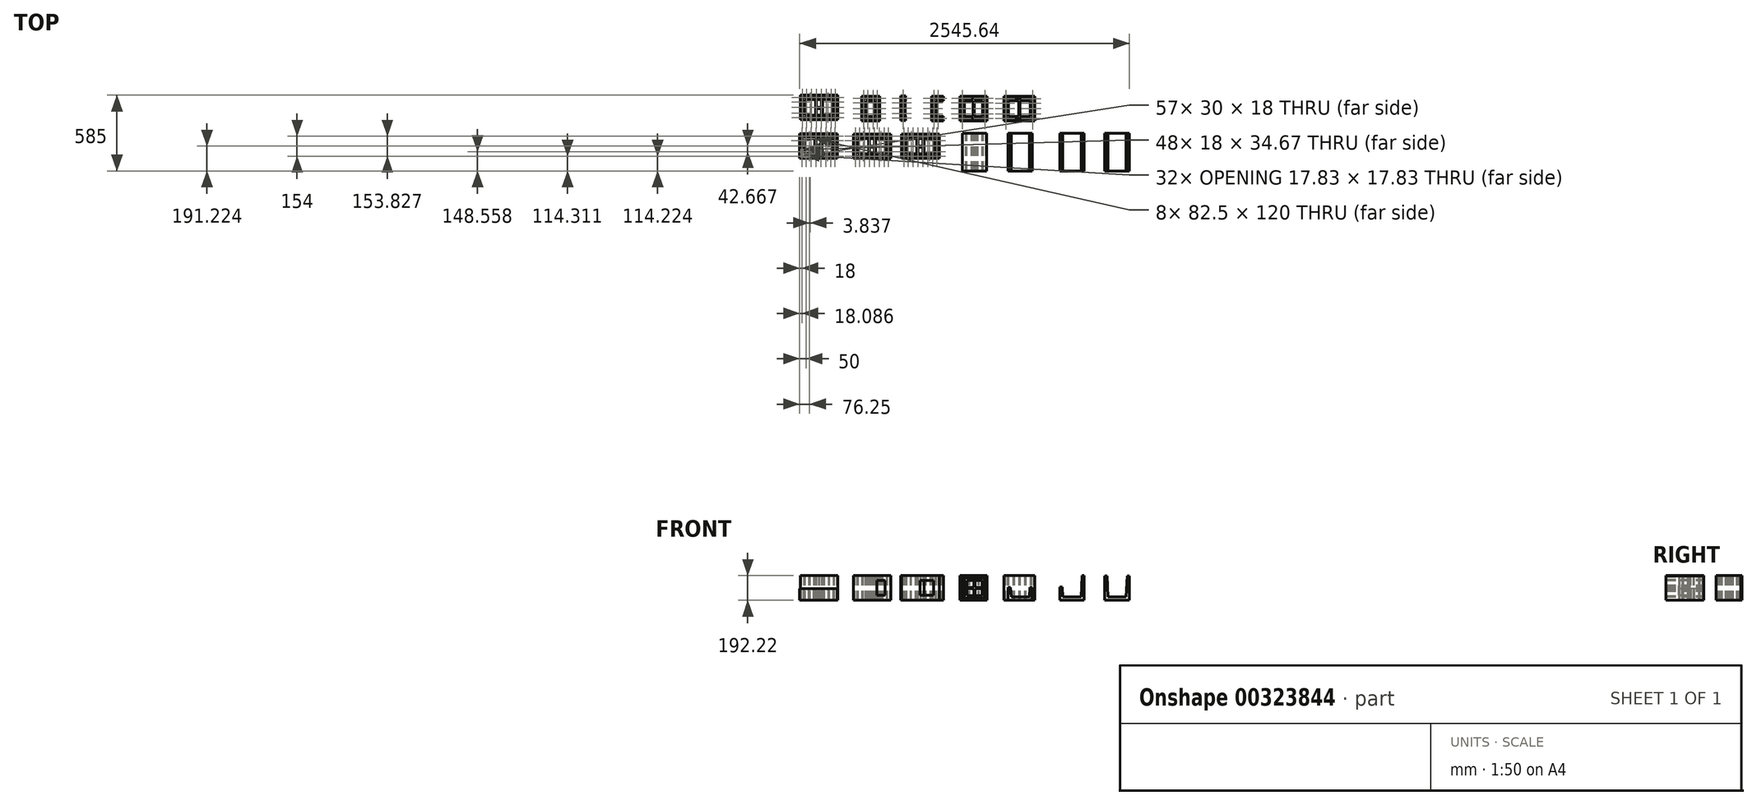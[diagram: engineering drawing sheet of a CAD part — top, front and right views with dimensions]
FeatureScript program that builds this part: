
annotation { "Feature Type Name" : "Feature", "Feature Type Description" : "" }
export const myFeature = defineFeature(function(context is Context, id is Id, definition is map)
    precondition{}
    {
        {
            var Q0;
            Q0=qCreatedBy(makeId("Top.planeOp"),FACE);
            var sketch = newSketch(context, id + "F0", { "sketchPlane" : qUnion([Q0])});
            skLineSegment(sketch, "E0", {"start": v(-906.96, 97) * mm, "end": v(-906.96, -93) * mm});
            skLineSegment(sketch, "E1", {"start": v(-906.96, -93) * mm, "end": v(-616.96, -93) * mm});
            skLineSegment(sketch, "E2", {"start": v(-616.96, -93) * mm, "end": v(-616.96, 97) * mm});
            skLineSegment(sketch, "E3", {"start": v(-616.96, 97) * mm, "end": v(-906.96, 97) * mm});
            skLineSegment(sketch, "E4", {"start": v(-871.96, 88) * mm, "end": v(-871.96, 70) * mm});
            skLineSegment(sketch, "E5", {"start": v(-871.96, 70) * mm, "end": v(-841.96, 70) * mm});
            skLineSegment(sketch, "E6", {"start": v(-841.96, 70) * mm, "end": v(-841.96, 88) * mm});
            skLineSegment(sketch, "E7", {"start": v(-841.96, 88) * mm, "end": v(-871.96, 88) * mm});
            skLineSegment(sketch, "E8", {"start": v(-833.96, 88) * mm, "end": v(-833.96, 70) * mm});
            skLineSegment(sketch, "E9", {"start": v(-833.96, 70) * mm, "end": v(-803.96, 70) * mm});
            skLineSegment(sketch, "E10", {"start": v(-803.96, 70) * mm, "end": v(-803.96, 88) * mm});
            skLineSegment(sketch, "E11", {"start": v(-803.96, 88) * mm, "end": v(-833.96, 88) * mm});
            skLineSegment(sketch, "E12", {"start": v(-795.96, 88) * mm, "end": v(-795.96, 70) * mm});
            skLineSegment(sketch, "E13", {"start": v(-795.96, 70) * mm, "end": v(-765.96, 70) * mm});
            skLineSegment(sketch, "E14", {"start": v(-765.96, 70) * mm, "end": v(-765.96, 88) * mm});
            skLineSegment(sketch, "E15", {"start": v(-765.96, 88) * mm, "end": v(-795.96, 88) * mm});
            skLineSegment(sketch, "E16", {"start": v(-757.96, 88) * mm, "end": v(-757.96, 70) * mm});
            skLineSegment(sketch, "E17", {"start": v(-757.96, 70) * mm, "end": v(-727.96, 70) * mm});
            skLineSegment(sketch, "E18", {"start": v(-727.96, 70) * mm, "end": v(-727.96, 88) * mm});
            skLineSegment(sketch, "E19", {"start": v(-727.96, 88) * mm, "end": v(-757.96, 88) * mm});
            skLineSegment(sketch, "E20", {"start": v(-719.96, 88) * mm, "end": v(-719.96, 70) * mm});
            skLineSegment(sketch, "E21", {"start": v(-719.96, 70) * mm, "end": v(-689.96, 70) * mm});
            skLineSegment(sketch, "E22", {"start": v(-689.96, 70) * mm, "end": v(-689.96, 88) * mm});
            skLineSegment(sketch, "E23", {"start": v(-689.96, 88) * mm, "end": v(-719.96, 88) * mm});
            skLineSegment(sketch, "E24", {"start": v(-681.96, 88) * mm, "end": v(-681.96, 70) * mm});
            skLineSegment(sketch, "E25", {"start": v(-681.96, 70) * mm, "end": v(-651.96, 70) * mm});
            skLineSegment(sketch, "E26", {"start": v(-651.96, 70) * mm, "end": v(-651.96, 88) * mm});
            skLineSegment(sketch, "E27", {"start": v(-651.96, 88) * mm, "end": v(-681.96, 88) * mm});
            skLineSegment(sketch, "E28", {"start": v(-643.96, 62) * mm, "end": v(-643.96, 27.33) * mm});
            skLineSegment(sketch, "E29", {"start": v(-643.96, 27.33) * mm, "end": v(-625.96, 27.33) * mm});
            skLineSegment(sketch, "E30", {"start": v(-625.96, 27.33) * mm, "end": v(-625.96, 62) * mm});
            skLineSegment(sketch, "E31", {"start": v(-625.96, 62) * mm, "end": v(-643.96, 62) * mm});
            skLineSegment(sketch, "E32", {"start": v(-897.96, 62) * mm, "end": v(-897.96, 27.33) * mm});
            skLineSegment(sketch, "E33", {"start": v(-897.96, 27.33) * mm, "end": v(-879.96, 27.33) * mm});
            skLineSegment(sketch, "E34", {"start": v(-879.96, 27.33) * mm, "end": v(-879.96, 62) * mm});
            skLineSegment(sketch, "E35", {"start": v(-879.96, 62) * mm, "end": v(-897.96, 62) * mm});
            skLineSegment(sketch, "E36", {"start": v(-897.96, 19.33) * mm, "end": v(-897.96, -15.33) * mm});
            skLineSegment(sketch, "E37", {"start": v(-897.96, -15.33) * mm, "end": v(-879.96, -15.33) * mm});
            skLineSegment(sketch, "E38", {"start": v(-879.96, -15.33) * mm, "end": v(-879.96, 19.33) * mm});
            skLineSegment(sketch, "E39", {"start": v(-879.96, 19.33) * mm, "end": v(-897.96, 19.33) * mm});
            skLineSegment(sketch, "E40", {"start": v(-897.96, -23.33) * mm, "end": v(-897.96, -58) * mm});
            skLineSegment(sketch, "E41", {"start": v(-897.96, -58) * mm, "end": v(-879.96, -58) * mm});
            skLineSegment(sketch, "E42", {"start": v(-879.96, -58) * mm, "end": v(-879.96, -23.33) * mm});
            skLineSegment(sketch, "E43", {"start": v(-879.96, -23.33) * mm, "end": v(-897.96, -23.33) * mm});
            skLineSegment(sketch, "E44", {"start": v(-871.96, -66) * mm, "end": v(-871.96, -84) * mm});
            skLineSegment(sketch, "E45", {"start": v(-871.96, -84) * mm, "end": v(-841.96, -84) * mm});
            skLineSegment(sketch, "E46", {"start": v(-841.96, -84) * mm, "end": v(-841.96, -66) * mm});
            skLineSegment(sketch, "E47", {"start": v(-841.96, -66) * mm, "end": v(-871.96, -66) * mm});
            skLineSegment(sketch, "E48", {"start": v(-833.96, -66) * mm, "end": v(-833.96, -84) * mm});
            skLineSegment(sketch, "E49", {"start": v(-833.96, -84) * mm, "end": v(-803.96, -84) * mm});
            skLineSegment(sketch, "E50", {"start": v(-803.96, -84) * mm, "end": v(-803.96, -66) * mm});
            skLineSegment(sketch, "E51", {"start": v(-803.96, -66) * mm, "end": v(-833.96, -66) * mm});
            skLineSegment(sketch, "E52", {"start": v(-871.96, 62) * mm, "end": v(-871.96, -58) * mm});
            skLineSegment(sketch, "E53", {"start": v(-871.96, -58) * mm, "end": v(-789.46, -58) * mm});
            skLineSegment(sketch, "E54", {"start": v(-789.46, -58) * mm, "end": v(-789.46, 62) * mm});
            skLineSegment(sketch, "E55", {"start": v(-789.46, 62) * mm, "end": v(-871.96, 62) * mm});
            skLineSegment(sketch, "E56", {"start": v(-795.96, -66) * mm, "end": v(-795.96, -84) * mm});
            skLineSegment(sketch, "E57", {"start": v(-795.96, -84) * mm, "end": v(-765.96, -84) * mm});
            skLineSegment(sketch, "E58", {"start": v(-765.96, -84) * mm, "end": v(-765.96, -66) * mm});
            skLineSegment(sketch, "E59", {"start": v(-765.96, -66) * mm, "end": v(-795.96, -66) * mm});
            skLineSegment(sketch, "E60", {"start": v(-757.96, -66) * mm, "end": v(-757.96, -84) * mm});
            skLineSegment(sketch, "E61", {"start": v(-757.96, -84) * mm, "end": v(-727.96, -84) * mm});
            skLineSegment(sketch, "E62", {"start": v(-727.96, -84) * mm, "end": v(-727.96, -66) * mm});
            skLineSegment(sketch, "E63", {"start": v(-727.96, -66) * mm, "end": v(-757.96, -66) * mm});
            skLineSegment(sketch, "E64", {"start": v(-719.96, -66) * mm, "end": v(-719.96, -84) * mm});
            skLineSegment(sketch, "E65", {"start": v(-719.96, -84) * mm, "end": v(-689.96, -84) * mm});
            skLineSegment(sketch, "E66", {"start": v(-689.96, -84) * mm, "end": v(-689.96, -66) * mm});
            skLineSegment(sketch, "E67", {"start": v(-689.96, -66) * mm, "end": v(-719.96, -66) * mm});
            skLineSegment(sketch, "E68", {"start": v(-681.96, -66) * mm, "end": v(-681.96, -84) * mm});
            skLineSegment(sketch, "E69", {"start": v(-681.96, -84) * mm, "end": v(-651.96, -84) * mm});
            skLineSegment(sketch, "E70", {"start": v(-651.96, -84) * mm, "end": v(-651.96, -66) * mm});
            skLineSegment(sketch, "E71", {"start": v(-651.96, -66) * mm, "end": v(-681.96, -66) * mm});
            skLineSegment(sketch, "E72", {"start": v(-643.96, -58) * mm, "end": v(-643.96, -23.33) * mm});
            skLineSegment(sketch, "E73", {"start": v(-643.96, -23.33) * mm, "end": v(-625.96, -23.33) * mm});
            skLineSegment(sketch, "E74", {"start": v(-625.96, -23.33) * mm, "end": v(-625.96, -58) * mm});
            skLineSegment(sketch, "E75", {"start": v(-625.96, -58) * mm, "end": v(-643.96, -58) * mm});
            skLineSegment(sketch, "E76", {"start": v(-625.96, -15.33) * mm, "end": v(-625.96, 19.33) * mm});
            skLineSegment(sketch, "E77", {"start": v(-625.96, 19.33) * mm, "end": v(-643.96, 19.33) * mm});
            skLineSegment(sketch, "E78", {"start": v(-643.96, 19.33) * mm, "end": v(-643.96, -15.33) * mm});
            skLineSegment(sketch, "E79", {"start": v(-643.96, -15.33) * mm, "end": v(-625.96, -15.33) * mm});
            skLineSegment(sketch, "E80", {"start": v(-734.46, 62) * mm, "end": v(-734.46, -58) * mm});
            skLineSegment(sketch, "E81", {"start": v(-734.46, -58) * mm, "end": v(-651.96, -58) * mm});
            skLineSegment(sketch, "E82", {"start": v(-651.96, -58) * mm, "end": v(-651.96, 62) * mm});
            skLineSegment(sketch, "E83", {"start": v(-651.96, 62) * mm, "end": v(-734.46, 62) * mm});
            skLineSegment(sketch, "E84", {"start": v(-742.46, -58) * mm, "end": v(-742.46, -6) * mm});
            skLineSegment(sketch, "E85", {"start": v(-742.46, -6) * mm, "end": v(-781.46, -6) * mm});
            skLineSegment(sketch, "E86", {"start": v(-781.46, -6) * mm, "end": v(-781.46, -58) * mm});
            skLineSegment(sketch, "E87", {"start": v(-781.46, -58) * mm, "end": v(-742.46, -58) * mm});
            skLineSegment(sketch, "E88", {"start": v(-781.46, 62) * mm, "end": v(-781.46, 2) * mm});
            skLineSegment(sketch, "E89", {"start": v(-781.46, 2) * mm, "end": v(-742.46, 2) * mm});
            skLineSegment(sketch, "E90", {"start": v(-742.46, 2) * mm, "end": v(-742.46, 62) * mm});
            skLineSegment(sketch, "E91", {"start": v(-742.46, 62) * mm, "end": v(-781.46, 62) * mm});
            skLineSegment(sketch, "E92", {"start": v(-433.37, 89.63) * mm, "end": v(-433.37, -100.37) * mm});
            skLineSegment(sketch, "E93", {"start": v(-433.37, -100.37) * mm, "end": v(-293.37, -100.37) * mm});
            skLineSegment(sketch, "E94", {"start": v(-293.37, -100.37) * mm, "end": v(-293.37, 89.63) * mm});
            skLineSegment(sketch, "E95", {"start": v(-293.37, 89.63) * mm, "end": v(-433.37, 89.63) * mm});
            skLineSegment(sketch, "E96", {"start": v(-424.37, 54.63) * mm, "end": v(-424.37, 19.96) * mm});
            skLineSegment(sketch, "E97", {"start": v(-424.37, 19.96) * mm, "end": v(-406.37, 19.96) * mm});
            skLineSegment(sketch, "E98", {"start": v(-406.37, 19.96) * mm, "end": v(-406.37, 54.63) * mm});
            skLineSegment(sketch, "E99", {"start": v(-406.37, 54.63) * mm, "end": v(-424.37, 54.63) * mm});
            skLineSegment(sketch, "E100", {"start": v(-424.37, 11.96) * mm, "end": v(-424.37, -22.7) * mm});
            skLineSegment(sketch, "E101", {"start": v(-424.37, -22.7) * mm, "end": v(-406.37, -22.7) * mm});
            skLineSegment(sketch, "E102", {"start": v(-406.37, -22.7) * mm, "end": v(-406.37, 11.96) * mm});
            skLineSegment(sketch, "E103", {"start": v(-406.37, 11.96) * mm, "end": v(-424.37, 11.96) * mm});
            skLineSegment(sketch, "E104", {"start": v(-424.37, -30.7) * mm, "end": v(-424.37, -65.37) * mm});
            skLineSegment(sketch, "E105", {"start": v(-424.37, -65.37) * mm, "end": v(-406.37, -65.37) * mm});
            skLineSegment(sketch, "E106", {"start": v(-406.37, -65.37) * mm, "end": v(-406.37, -30.7) * mm});
            skLineSegment(sketch, "E107", {"start": v(-406.37, -30.7) * mm, "end": v(-424.37, -30.7) * mm});
            skLineSegment(sketch, "E108", {"start": v(-398.37, -73.37) * mm, "end": v(-398.37, -91.37) * mm});
            skLineSegment(sketch, "E109", {"start": v(-398.37, -91.37) * mm, "end": v(-368.37, -91.37) * mm});
            skLineSegment(sketch, "E110", {"start": v(-368.37, -91.37) * mm, "end": v(-368.37, -73.37) * mm});
            skLineSegment(sketch, "E111", {"start": v(-368.37, -73.37) * mm, "end": v(-398.37, -73.37) * mm});
            skLineSegment(sketch, "E112", {"start": v(-358.37, -73.37) * mm, "end": v(-358.37, -91.37) * mm});
            skLineSegment(sketch, "E113", {"start": v(-358.37, -91.37) * mm, "end": v(-328.37, -91.37) * mm});
            skLineSegment(sketch, "E114", {"start": v(-328.37, -91.37) * mm, "end": v(-328.37, -73.37) * mm});
            skLineSegment(sketch, "E115", {"start": v(-328.37, -73.37) * mm, "end": v(-358.37, -73.37) * mm});
            skLineSegment(sketch, "E116", {"start": v(-320.37, 54.63) * mm, "end": v(-320.37, 19.96) * mm});
            skLineSegment(sketch, "E117", {"start": v(-320.37, 19.96) * mm, "end": v(-302.37, 19.96) * mm});
            skLineSegment(sketch, "E118", {"start": v(-302.37, 19.96) * mm, "end": v(-302.37, 54.63) * mm});
            skLineSegment(sketch, "E119", {"start": v(-302.37, 54.63) * mm, "end": v(-320.37, 54.63) * mm});
            skLineSegment(sketch, "E120", {"start": v(-320.37, 11.96) * mm, "end": v(-320.37, -22.7) * mm});
            skLineSegment(sketch, "E121", {"start": v(-320.37, -22.7) * mm, "end": v(-302.37, -22.7) * mm});
            skLineSegment(sketch, "E122", {"start": v(-302.37, -22.7) * mm, "end": v(-302.37, 11.96) * mm});
            skLineSegment(sketch, "E123", {"start": v(-302.37, 11.96) * mm, "end": v(-320.37, 11.96) * mm});
            skLineSegment(sketch, "E124", {"start": v(-320.37, -30.7) * mm, "end": v(-320.37, -65.37) * mm});
            skLineSegment(sketch, "E125", {"start": v(-320.37, -65.37) * mm, "end": v(-302.37, -65.37) * mm});
            skLineSegment(sketch, "E126", {"start": v(-302.37, -65.37) * mm, "end": v(-302.37, -30.7) * mm});
            skLineSegment(sketch, "E127", {"start": v(-302.37, -30.7) * mm, "end": v(-320.37, -30.7) * mm});
            skLineSegment(sketch, "E128", {"start": v(-398.37, 54.63) * mm, "end": v(-398.37, -65.37) * mm});
            skLineSegment(sketch, "E129", {"start": v(-398.37, -65.37) * mm, "end": v(-328.37, -65.37) * mm});
            skLineSegment(sketch, "E130", {"start": v(-328.37, -65.37) * mm, "end": v(-328.37, 54.63) * mm});
            skLineSegment(sketch, "E131", {"start": v(-328.37, 54.63) * mm, "end": v(-398.37, 54.63) * mm});
            skLineSegment(sketch, "E132", {"start": v(-398.37, 80.63) * mm, "end": v(-398.37, 62.63) * mm});
            skLineSegment(sketch, "E133", {"start": v(-398.37, 62.63) * mm, "end": v(-368.37, 62.63) * mm});
            skLineSegment(sketch, "E134", {"start": v(-368.37, 62.63) * mm, "end": v(-368.37, 80.63) * mm});
            skLineSegment(sketch, "E135", {"start": v(-368.37, 80.63) * mm, "end": v(-398.37, 80.63) * mm});
            skLineSegment(sketch, "E136", {"start": v(-358.37, 62.63) * mm, "end": v(-358.37, 80.63) * mm});
            skLineSegment(sketch, "E137", {"start": v(-358.37, 80.63) * mm, "end": v(-328.37, 80.63) * mm});
            skLineSegment(sketch, "E138", {"start": v(-328.37, 80.63) * mm, "end": v(-328.37, 62.63) * mm});
            skLineSegment(sketch, "E139", {"start": v(-328.37, 62.63) * mm, "end": v(-358.37, 62.63) * mm});
            skLineSegment(sketch, "E140", {"start": v(-122.36, 56.55) * mm, "end": v(-122.36, 21.88) * mm});
            skLineSegment(sketch, "E141", {"start": v(-122.36, 21.88) * mm, "end": v(-104.36, 21.88) * mm});
            skLineSegment(sketch, "E142", {"start": v(-104.36, 21.88) * mm, "end": v(-104.36, 56.55) * mm});
            skLineSegment(sketch, "E143", {"start": v(-104.36, 56.55) * mm, "end": v(-122.36, 56.55) * mm});
            skLineSegment(sketch, "E144", {"start": v(-122.36, 13.88) * mm, "end": v(-122.36, -20.78) * mm});
            skLineSegment(sketch, "E145", {"start": v(-122.36, -20.78) * mm, "end": v(-104.36, -20.78) * mm});
            skLineSegment(sketch, "E146", {"start": v(-104.36, -20.78) * mm, "end": v(-104.36, 13.88) * mm});
            skLineSegment(sketch, "E147", {"start": v(-104.36, 13.88) * mm, "end": v(-122.36, 13.88) * mm});
            skLineSegment(sketch, "E148", {"start": v(-122.36, -28.78) * mm, "end": v(-122.36, -63.45) * mm});
            skLineSegment(sketch, "E149", {"start": v(-122.36, -63.45) * mm, "end": v(-104.36, -63.45) * mm});
            skLineSegment(sketch, "E150", {"start": v(-104.36, -63.45) * mm, "end": v(-104.36, -28.78) * mm});
            skLineSegment(sketch, "E151", {"start": v(-104.36, -28.78) * mm, "end": v(-122.36, -28.78) * mm});
            skLineSegment(sketch, "E152", {"start": v(-131.36, -98.45) * mm, "end": v(-131.36, 91.55) * mm});
            skLineSegment(sketch, "E153", {"start": v(-131.36, 91.55) * mm, "end": v(-91.36, 91.55) * mm});
            skLineSegment(sketch, "E154", {"start": v(-91.36, 91.55) * mm, "end": v(-91.36, 82.55) * mm});
            skLineSegment(sketch, "E155", {"start": v(-91.36, 82.55) * mm, "end": v(-96.36, 82.55) * mm});
            skLineSegment(sketch, "E156", {"start": v(-96.36, 82.55) * mm, "end": v(-96.36, 64.55) * mm});
            skLineSegment(sketch, "E157", {"start": v(-96.36, 64.55) * mm, "end": v(-91.36, 64.55) * mm});
            skLineSegment(sketch, "E158", {"start": v(-91.36, 64.55) * mm, "end": v(-91.36, 56.55) * mm});
            skLineSegment(sketch, "E159", {"start": v(-91.36, 56.55) * mm, "end": v(-96.36, 56.55) * mm});
            skLineSegment(sketch, "E160", {"start": v(-96.36, 56.55) * mm, "end": v(-96.36, -63.45) * mm});
            skLineSegment(sketch, "E161", {"start": v(-96.36, -63.45) * mm, "end": v(-91.36, -63.45) * mm});
            skLineSegment(sketch, "E162", {"start": v(-91.36, -63.45) * mm, "end": v(-91.36, -71.45) * mm});
            skLineSegment(sketch, "E163", {"start": v(-91.36, -71.45) * mm, "end": v(-96.36, -71.45) * mm});
            skLineSegment(sketch, "E164", {"start": v(-96.36, -71.45) * mm, "end": v(-96.36, -89.45) * mm});
            skLineSegment(sketch, "E165", {"start": v(-96.36, -89.45) * mm, "end": v(-91.36, -89.45) * mm});
            skLineSegment(sketch, "E166", {"start": v(-91.36, -89.45) * mm, "end": v(-91.36, -98.45) * mm});
            skLineSegment(sketch, "E167", {"start": v(-91.36, -98.45) * mm, "end": v(-131.36, -98.45) * mm});
            skLineSegment(sketch, "E168", {"start": v(198.64, 89.49) * mm, "end": v(108.64, 89.49) * mm});
            skLineSegment(sketch, "E169", {"start": v(108.64, 89.49) * mm, "end": v(108.64, -100.51) * mm});
            skLineSegment(sketch, "E170", {"start": v(108.64, -100.51) * mm, "end": v(198.64, -100.51) * mm});
            skLineSegment(sketch, "E171", {"start": v(198.64, -100.51) * mm, "end": v(198.64, -91.51) * mm});
            skLineSegment(sketch, "E172", {"start": v(198.64, -91.51) * mm, "end": v(181.64, -91.51) * mm});
            skLineSegment(sketch, "E173", {"start": v(181.64, -91.51) * mm, "end": v(181.64, -73.51) * mm});
            skLineSegment(sketch, "E174", {"start": v(181.64, -73.51) * mm, "end": v(198.64, -73.51) * mm});
            skLineSegment(sketch, "E175", {"start": v(198.64, -73.51) * mm, "end": v(198.64, -65.51) * mm});
            skLineSegment(sketch, "E176", {"start": v(198.64, -65.51) * mm, "end": v(143.64, -65.51) * mm});
            skLineSegment(sketch, "E177", {"start": v(143.64, -65.51) * mm, "end": v(143.64, 54.49) * mm});
            skLineSegment(sketch, "E178", {"start": v(143.64, 54.49) * mm, "end": v(198.64, 54.49) * mm});
            skLineSegment(sketch, "E179", {"start": v(198.64, 54.49) * mm, "end": v(198.64, 62.49) * mm});
            skLineSegment(sketch, "E180", {"start": v(198.64, 62.49) * mm, "end": v(181.64, 62.49) * mm});
            skLineSegment(sketch, "E181", {"start": v(181.64, 62.49) * mm, "end": v(181.64, 80.49) * mm});
            skLineSegment(sketch, "E182", {"start": v(181.64, 80.49) * mm, "end": v(198.64, 80.49) * mm});
            skLineSegment(sketch, "E183", {"start": v(198.64, 80.49) * mm, "end": v(198.64, 89.49) * mm});
            skLineSegment(sketch, "E184", {"start": v(143.64, 80.49) * mm, "end": v(143.64, 62.49) * mm});
            skLineSegment(sketch, "E185", {"start": v(143.64, 62.49) * mm, "end": v(173.64, 62.49) * mm});
            skLineSegment(sketch, "E186", {"start": v(173.64, 62.49) * mm, "end": v(173.64, 80.49) * mm});
            skLineSegment(sketch, "E187", {"start": v(173.64, 80.49) * mm, "end": v(143.64, 80.49) * mm});
            skLineSegment(sketch, "E188", {"start": v(117.64, 54.49) * mm, "end": v(117.64, 19.82) * mm});
            skLineSegment(sketch, "E189", {"start": v(117.64, 19.82) * mm, "end": v(135.64, 19.82) * mm});
            skLineSegment(sketch, "E190", {"start": v(135.64, 19.82) * mm, "end": v(135.64, 54.49) * mm});
            skLineSegment(sketch, "E191", {"start": v(135.64, 54.49) * mm, "end": v(117.64, 54.49) * mm});
            skLineSegment(sketch, "E192", {"start": v(117.64, 11.82) * mm, "end": v(117.64, -22.85) * mm});
            skLineSegment(sketch, "E193", {"start": v(117.64, -22.85) * mm, "end": v(135.64, -22.85) * mm});
            skLineSegment(sketch, "E194", {"start": v(135.64, -22.85) * mm, "end": v(135.64, 11.82) * mm});
            skLineSegment(sketch, "E195", {"start": v(135.64, 11.82) * mm, "end": v(117.64, 11.82) * mm});
            skLineSegment(sketch, "E196", {"start": v(117.64, -30.85) * mm, "end": v(117.64, -65.51) * mm});
            skLineSegment(sketch, "E197", {"start": v(117.64, -65.51) * mm, "end": v(135.64, -65.51) * mm});
            skLineSegment(sketch, "E198", {"start": v(135.64, -65.51) * mm, "end": v(135.64, -30.85) * mm});
            skLineSegment(sketch, "E199", {"start": v(135.64, -30.85) * mm, "end": v(117.64, -30.85) * mm});
            skLineSegment(sketch, "E200", {"start": v(143.64, -73.51) * mm, "end": v(143.64, -91.51) * mm});
            skLineSegment(sketch, "E201", {"start": v(143.64, -91.51) * mm, "end": v(173.64, -91.51) * mm});
            skLineSegment(sketch, "E202", {"start": v(173.64, -91.51) * mm, "end": v(173.64, -73.51) * mm});
            skLineSegment(sketch, "E203", {"start": v(173.64, -73.51) * mm, "end": v(143.64, -73.51) * mm});
            skLineSegment(sketch, "E204", {"start": v(327.12, 89.6) * mm, "end": v(327.12, -100.4) * mm});
            skLineSegment(sketch, "E205", {"start": v(327.12, -100.4) * mm, "end": v(537.12, -100.4) * mm});
            skLineSegment(sketch, "E206", {"start": v(537.12, -100.4) * mm, "end": v(537.12, 89.6) * mm});
            skLineSegment(sketch, "E207", {"start": v(537.12, 89.6) * mm, "end": v(327.12, 89.6) * mm});
            skLineSegment(sketch, "E208", {"start": v(436.12, 54.6) * mm, "end": v(436.12, -65.4) * mm});
            skLineSegment(sketch, "E209", {"start": v(436.12, -65.4) * mm, "end": v(502.12, -65.4) * mm});
            skLineSegment(sketch, "E210", {"start": v(502.12, -65.4) * mm, "end": v(502.12, 54.6) * mm});
            skLineSegment(sketch, "E211", {"start": v(502.12, 54.6) * mm, "end": v(436.12, 54.6) * mm});
            skLineSegment(sketch, "E212", {"start": v(428.12, 54.6) * mm, "end": v(428.12, -65.4) * mm});
            skLineSegment(sketch, "E213", {"start": v(428.12, -65.4) * mm, "end": v(362.12, -65.4) * mm});
            skLineSegment(sketch, "E214", {"start": v(362.12, -65.4) * mm, "end": v(362.12, 54.6) * mm});
            skLineSegment(sketch, "E215", {"start": v(362.12, 54.6) * mm, "end": v(428.12, 54.6) * mm});
            skLineSegment(sketch, "E216", {"start": v(362.12, 80.6) * mm, "end": v(362.12, 62.6) * mm});
            skLineSegment(sketch, "E217", {"start": v(362.12, 62.6) * mm, "end": v(391.24, 62.6) * mm});
            skLineSegment(sketch, "E218", {"start": v(391.24, 62.6) * mm, "end": v(391.24, 80.6) * mm});
            skLineSegment(sketch, "E219", {"start": v(391.24, 80.6) * mm, "end": v(362.12, 80.6) * mm});
            skLineSegment(sketch, "E220", {"start": v(399, 62.6) * mm, "end": v(399, 80.6) * mm});
            skLineSegment(sketch, "E221", {"start": v(399, 80.6) * mm, "end": v(428.12, 80.6) * mm});
            skLineSegment(sketch, "E222", {"start": v(428.12, 80.6) * mm, "end": v(428.12, 62.6) * mm});
            skLineSegment(sketch, "E223", {"start": v(428.12, 62.6) * mm, "end": v(399, 62.6) * mm});
            skLineSegment(sketch, "E224", {"start": v(436.12, 80.6) * mm, "end": v(436.12, 62.6) * mm});
            skLineSegment(sketch, "E225", {"start": v(436.12, 62.6) * mm, "end": v(465.24, 62.6) * mm});
            skLineSegment(sketch, "E226", {"start": v(465.24, 62.6) * mm, "end": v(465.24, 80.6) * mm});
            skLineSegment(sketch, "E227", {"start": v(465.24, 80.6) * mm, "end": v(436.12, 80.6) * mm});
            skLineSegment(sketch, "E228", {"start": v(473, 62.6) * mm, "end": v(473, 80.6) * mm});
            skLineSegment(sketch, "E229", {"start": v(473, 80.6) * mm, "end": v(502.12, 80.6) * mm});
            skLineSegment(sketch, "E230", {"start": v(502.12, 80.6) * mm, "end": v(502.12, 62.6) * mm});
            skLineSegment(sketch, "E231", {"start": v(502.12, 62.6) * mm, "end": v(473, 62.6) * mm});
            skLineSegment(sketch, "E232", {"start": v(510.12, 54.6) * mm, "end": v(510.12, 19.93) * mm});
            skLineSegment(sketch, "E233", {"start": v(510.12, 19.93) * mm, "end": v(528.12, 19.93) * mm});
            skLineSegment(sketch, "E234", {"start": v(528.12, 19.93) * mm, "end": v(528.12, 54.6) * mm});
            skLineSegment(sketch, "E235", {"start": v(528.12, 54.6) * mm, "end": v(510.12, 54.6) * mm});
            skLineSegment(sketch, "E236", {"start": v(528.12, 11.93) * mm, "end": v(528.12, -22.74) * mm});
            skLineSegment(sketch, "E237", {"start": v(528.12, -22.74) * mm, "end": v(510.12, -22.74) * mm});
            skLineSegment(sketch, "E238", {"start": v(510.12, -22.74) * mm, "end": v(510.12, 11.93) * mm});
            skLineSegment(sketch, "E239", {"start": v(510.12, 11.93) * mm, "end": v(528.12, 11.93) * mm});
            skLineSegment(sketch, "E240", {"start": v(510.12, -30.74) * mm, "end": v(510.12, -65.4) * mm});
            skLineSegment(sketch, "E241", {"start": v(510.12, -65.4) * mm, "end": v(528.12, -65.4) * mm});
            skLineSegment(sketch, "E242", {"start": v(528.12, -65.4) * mm, "end": v(528.12, -30.74) * mm});
            skLineSegment(sketch, "E243", {"start": v(528.12, -30.74) * mm, "end": v(510.12, -30.74) * mm});
            skLineSegment(sketch, "E244", {"start": v(502.12, -73.4) * mm, "end": v(502.12, -91.4) * mm});
            skLineSegment(sketch, "E245", {"start": v(502.12, -91.4) * mm, "end": v(473, -91.4) * mm});
            skLineSegment(sketch, "E246", {"start": v(473, -91.4) * mm, "end": v(473, -73.4) * mm});
            skLineSegment(sketch, "E247", {"start": v(473, -73.4) * mm, "end": v(502.12, -73.4) * mm});
            skLineSegment(sketch, "E248", {"start": v(465.24, -91.4) * mm, "end": v(465.24, -73.4) * mm});
            skLineSegment(sketch, "E249", {"start": v(465.24, -73.4) * mm, "end": v(436.12, -73.4) * mm});
            skLineSegment(sketch, "E250", {"start": v(436.12, -73.4) * mm, "end": v(436.12, -91.4) * mm});
            skLineSegment(sketch, "E251", {"start": v(436.12, -91.4) * mm, "end": v(465.24, -91.4) * mm});
            skLineSegment(sketch, "E252", {"start": v(428.12, -91.4) * mm, "end": v(428.12, -73.4) * mm});
            skLineSegment(sketch, "E253", {"start": v(428.12, -73.4) * mm, "end": v(399, -73.4) * mm});
            skLineSegment(sketch, "E254", {"start": v(399, -73.4) * mm, "end": v(399, -91.4) * mm});
            skLineSegment(sketch, "E255", {"start": v(399, -91.4) * mm, "end": v(428.12, -91.4) * mm});
            skLineSegment(sketch, "E256", {"start": v(362.12, -73.4) * mm, "end": v(362.12, -91.4) * mm});
            skLineSegment(sketch, "E257", {"start": v(362.12, -91.4) * mm, "end": v(391.24, -91.4) * mm});
            skLineSegment(sketch, "E258", {"start": v(391.24, -91.4) * mm, "end": v(391.24, -73.4) * mm});
            skLineSegment(sketch, "E259", {"start": v(391.24, -73.4) * mm, "end": v(362.12, -73.4) * mm});
            skLineSegment(sketch, "E260", {"start": v(354.12, -65.4) * mm, "end": v(354.12, -30.74) * mm});
            skLineSegment(sketch, "E261", {"start": v(354.12, -30.74) * mm, "end": v(336.12, -30.74) * mm});
            skLineSegment(sketch, "E262", {"start": v(336.12, -30.74) * mm, "end": v(336.12, -65.4) * mm});
            skLineSegment(sketch, "E263", {"start": v(336.12, -65.4) * mm, "end": v(354.12, -65.4) * mm});
            skLineSegment(sketch, "E264", {"start": v(336.12, -22.74) * mm, "end": v(336.12, 11.93) * mm});
            skLineSegment(sketch, "E265", {"start": v(336.12, 11.93) * mm, "end": v(354.12, 11.93) * mm});
            skLineSegment(sketch, "E266", {"start": v(354.12, 11.93) * mm, "end": v(354.12, -22.74) * mm});
            skLineSegment(sketch, "E267", {"start": v(354.12, -22.74) * mm, "end": v(336.12, -22.74) * mm});
            skLineSegment(sketch, "E268", {"start": v(354.12, 19.93) * mm, "end": v(354.12, 54.6) * mm});
            skLineSegment(sketch, "E269", {"start": v(354.12, 54.6) * mm, "end": v(336.12, 54.6) * mm});
            skLineSegment(sketch, "E270", {"start": v(336.12, 54.6) * mm, "end": v(336.12, 19.93) * mm});
            skLineSegment(sketch, "E271", {"start": v(336.12, 19.93) * mm, "end": v(354.12, 19.93) * mm});
            skLineSegment(sketch, "E272", {"start": v(665.08, 88.4) * mm, "end": v(665.08, -101.6) * mm});
            skLineSegment(sketch, "E273", {"start": v(665.08, -101.6) * mm, "end": v(905.08, -101.6) * mm});
            skLineSegment(sketch, "E274", {"start": v(905.08, -101.6) * mm, "end": v(905.08, 88.4) * mm});
            skLineSegment(sketch, "E275", {"start": v(905.08, 88.4) * mm, "end": v(665.08, 88.4) * mm});
            skLineSegment(sketch, "E276", {"start": v(870.08, -66.6) * mm, "end": v(870.08, 53.4) * mm});
            skLineSegment(sketch, "E277", {"start": v(870.08, 53.4) * mm, "end": v(789.08, 53.4) * mm});
            skLineSegment(sketch, "E278", {"start": v(789.08, 53.4) * mm, "end": v(789.08, -66.6) * mm});
            skLineSegment(sketch, "E279", {"start": v(789.08, -66.6) * mm, "end": v(870.08, -66.6) * mm});
            skLineSegment(sketch, "E280", {"start": v(781.08, 53.4) * mm, "end": v(781.08, -66.6) * mm});
            skLineSegment(sketch, "E281", {"start": v(781.08, -66.6) * mm, "end": v(700.08, -66.6) * mm});
            skLineSegment(sketch, "E282", {"start": v(700.08, -66.6) * mm, "end": v(700.08, 53.4) * mm});
            skLineSegment(sketch, "E283", {"start": v(700.08, 53.4) * mm, "end": v(781.08, 53.4) * mm});
            skLineSegment(sketch, "E284", {"start": v(674.08, -66.6) * mm, "end": v(674.08, -31.94) * mm});
            skLineSegment(sketch, "E285", {"start": v(674.08, -31.94) * mm, "end": v(692.08, -31.94) * mm});
            skLineSegment(sketch, "E286", {"start": v(692.08, -31.94) * mm, "end": v(692.08, -66.6) * mm});
            skLineSegment(sketch, "E287", {"start": v(692.08, -66.6) * mm, "end": v(674.08, -66.6) * mm});
            skLineSegment(sketch, "E288", {"start": v(692.08, -23.94) * mm, "end": v(692.08, 10.73) * mm});
            skLineSegment(sketch, "E289", {"start": v(692.08, 10.73) * mm, "end": v(674.08, 10.73) * mm});
            skLineSegment(sketch, "E290", {"start": v(674.08, 10.73) * mm, "end": v(674.08, -23.94) * mm});
            skLineSegment(sketch, "E291", {"start": v(674.08, -23.94) * mm, "end": v(692.08, -23.94) * mm});
            skLineSegment(sketch, "E292", {"start": v(700.08, -74.6) * mm, "end": v(700.08, -92.6) * mm});
            skLineSegment(sketch, "E293", {"start": v(700.08, -92.6) * mm, "end": v(735.82, -92.6) * mm});
            skLineSegment(sketch, "E294", {"start": v(735.82, -92.6) * mm, "end": v(735.82, -74.6) * mm});
            skLineSegment(sketch, "E295", {"start": v(735.82, -74.6) * mm, "end": v(700.08, -74.6) * mm});
            skLineSegment(sketch, "E296", {"start": v(745.35, -74.6) * mm, "end": v(745.35, -92.6) * mm});
            skLineSegment(sketch, "E297", {"start": v(745.35, -92.6) * mm, "end": v(781.08, -92.6) * mm});
            skLineSegment(sketch, "E298", {"start": v(781.08, -92.6) * mm, "end": v(781.08, -74.6) * mm});
            skLineSegment(sketch, "E299", {"start": v(781.08, -74.6) * mm, "end": v(745.35, -74.6) * mm});
            skLineSegment(sketch, "E300", {"start": v(789.08, -74.6) * mm, "end": v(789.08, -92.6) * mm});
            skLineSegment(sketch, "E301", {"start": v(789.08, -92.6) * mm, "end": v(824.82, -92.6) * mm});
            skLineSegment(sketch, "E302", {"start": v(824.82, -92.6) * mm, "end": v(824.82, -74.6) * mm});
            skLineSegment(sketch, "E303", {"start": v(824.82, -74.6) * mm, "end": v(789.08, -74.6) * mm});
            skLineSegment(sketch, "E304", {"start": v(834.35, -74.6) * mm, "end": v(834.35, -92.6) * mm});
            skLineSegment(sketch, "E305", {"start": v(834.35, -92.6) * mm, "end": v(870.08, -92.6) * mm});
            skLineSegment(sketch, "E306", {"start": v(870.08, -92.6) * mm, "end": v(870.08, -74.6) * mm});
            skLineSegment(sketch, "E307", {"start": v(870.08, -74.6) * mm, "end": v(834.35, -74.6) * mm});
            skLineSegment(sketch, "E308", {"start": v(878.08, -31.94) * mm, "end": v(878.08, -66.6) * mm});
            skLineSegment(sketch, "E309", {"start": v(878.08, -66.6) * mm, "end": v(896.08, -66.6) * mm});
            skLineSegment(sketch, "E310", {"start": v(896.08, -66.6) * mm, "end": v(896.08, -31.94) * mm});
            skLineSegment(sketch, "E311", {"start": v(896.08, -31.94) * mm, "end": v(878.08, -31.94) * mm});
            skLineSegment(sketch, "E312", {"start": v(878.08, 10.73) * mm, "end": v(878.08, -23.94) * mm});
            skLineSegment(sketch, "E313", {"start": v(878.08, -23.94) * mm, "end": v(896.08, -23.94) * mm});
            skLineSegment(sketch, "E314", {"start": v(896.08, -23.94) * mm, "end": v(896.08, 10.73) * mm});
            skLineSegment(sketch, "E315", {"start": v(896.08, 10.73) * mm, "end": v(878.08, 10.73) * mm});
            skLineSegment(sketch, "E316", {"start": v(878.08, 53.4) * mm, "end": v(878.08, 18.73) * mm});
            skLineSegment(sketch, "E317", {"start": v(878.08, 18.73) * mm, "end": v(896.08, 18.73) * mm});
            skLineSegment(sketch, "E318", {"start": v(896.08, 18.73) * mm, "end": v(896.08, 53.4) * mm});
            skLineSegment(sketch, "E319", {"start": v(896.08, 53.4) * mm, "end": v(878.08, 53.4) * mm});
            skLineSegment(sketch, "E320", {"start": v(674.08, 53.4) * mm, "end": v(674.08, 18.73) * mm});
            skLineSegment(sketch, "E321", {"start": v(674.08, 18.73) * mm, "end": v(692.08, 18.73) * mm});
            skLineSegment(sketch, "E322", {"start": v(692.08, 18.73) * mm, "end": v(692.08, 53.4) * mm});
            skLineSegment(sketch, "E323", {"start": v(692.08, 53.4) * mm, "end": v(674.08, 53.4) * mm});
            skLineSegment(sketch, "E324", {"start": v(700.08, 79.4) * mm, "end": v(700.08, 61.4) * mm});
            skLineSegment(sketch, "E325", {"start": v(700.08, 61.4) * mm, "end": v(735.82, 61.4) * mm});
            skLineSegment(sketch, "E326", {"start": v(735.82, 61.4) * mm, "end": v(735.82, 79.4) * mm});
            skLineSegment(sketch, "E327", {"start": v(735.82, 79.4) * mm, "end": v(700.08, 79.4) * mm});
            skLineSegment(sketch, "E328", {"start": v(745.35, 79.4) * mm, "end": v(745.35, 61.4) * mm});
            skLineSegment(sketch, "E329", {"start": v(745.35, 61.4) * mm, "end": v(781.08, 61.4) * mm});
            skLineSegment(sketch, "E330", {"start": v(781.08, 61.4) * mm, "end": v(781.08, 79.4) * mm});
            skLineSegment(sketch, "E331", {"start": v(781.08, 79.4) * mm, "end": v(745.35, 79.4) * mm});
            skLineSegment(sketch, "E332", {"start": v(789.08, 79.4) * mm, "end": v(789.08, 61.4) * mm});
            skLineSegment(sketch, "E333", {"start": v(789.08, 61.4) * mm, "end": v(824.82, 61.4) * mm});
            skLineSegment(sketch, "E334", {"start": v(824.82, 61.4) * mm, "end": v(824.82, 79.4) * mm});
            skLineSegment(sketch, "E335", {"start": v(824.82, 79.4) * mm, "end": v(789.08, 79.4) * mm});
            skLineSegment(sketch, "E336", {"start": v(834.35, 79.4) * mm, "end": v(834.35, 61.4) * mm});
            skLineSegment(sketch, "E337", {"start": v(834.35, 61.4) * mm, "end": v(870.08, 61.4) * mm});
            skLineSegment(sketch, "E338", {"start": v(870.08, 61.4) * mm, "end": v(870.08, 79.4) * mm});
            skLineSegment(sketch, "E339", {"start": v(870.08, 79.4) * mm, "end": v(834.35, 79.4) * mm});
            skArc(sketch, "E340.cCircle", {"start": v(-879.96, 79) * mm, "mid": v(-895.33, 85.36) * mm, "end": v(-888.96, 70) * mm});
            skPoint(sketch, "E340.cCircle.centerSnap0", {"position": v(-888.96, 62) * mm});
            skPoint(sketch, "E340.cCircle.centerSnap1", {"position": v(-871.96, 79) * mm});
            skLineSegment(sketch, "E340.1", {"start": v(-879.96, 79) * mm, "end": v(-879.96, 70) * mm});
            skLineSegment(sketch, "E340.2", {"start": v(-879.96, 70) * mm, "end": v(-888.96, 70) * mm});
            skPoint(sketch, "E340.0.midPoint", {"position": v(-888.96, 88) * mm});
            skPoint(sketch, "E341.orphan", {"position": v(-897.96, 88) * mm});
            skPoint(sketch, "E340.0.end.orphan", {"position": v(-879.96, 88) * mm});
            skArc(sketch, "E342.cCircle", {"start": v(-888.96, -66) * mm, "mid": v(-895.33, -81.36) * mm, "end": v(-879.96, -75) * mm});
            skPoint(sketch, "E342.cCircle.centerSnap0", {"position": v(-871.96, -75) * mm});
            skPoint(sketch, "E342.cCircle.centerSnap1", {"position": v(-888.96, -58) * mm});
            skLineSegment(sketch, "E342.2", {"start": v(-888.96, -66) * mm, "end": v(-879.96, -66) * mm});
            skLineSegment(sketch, "E342.3", {"start": v(-879.96, -66) * mm, "end": v(-879.96, -75) * mm});
            skPoint(sketch, "E342.0.midPoint", {"position": v(-888.96, -84) * mm});
            skPoint(sketch, "E343.orphan", {"position": v(-897.96, -66) * mm});
            skPoint(sketch, "E344.orphan", {"position": v(-897.96, -84) * mm});
            skPoint(sketch, "E345.orphan", {"position": v(-879.96, -84) * mm});
            skArc(sketch, "E346.cCircle", {"start": v(-643.96, -75) * mm, "mid": v(-628.6, -81.36) * mm, "end": v(-634.96, -66) * mm});
            skPoint(sketch, "E346.cCircle.centerSnap0", {"position": v(-634.96, -58) * mm});
            skPoint(sketch, "E346.cCircle.centerSnap1", {"position": v(-651.96, -75) * mm});
            skLineSegment(sketch, "E346.1", {"start": v(-643.96, -75) * mm, "end": v(-643.96, -66) * mm});
            skLineSegment(sketch, "E346.2", {"start": v(-643.96, -66) * mm, "end": v(-634.96, -66) * mm});
            skPoint(sketch, "E346.0.midPoint", {"position": v(-634.96, -84) * mm});
            skPoint(sketch, "E347.orphan", {"position": v(-643.96, -84) * mm});
            skPoint(sketch, "E348.orphan", {"position": v(-625.96, -84) * mm});
            skArc(sketch, "E349.cCircle", {"start": v(-634.96, 70) * mm, "mid": v(-628.6, 85.36) * mm, "end": v(-643.96, 79) * mm});
            skPoint(sketch, "E349.cCircle.centerSnap0", {"position": v(-634.96, 62) * mm});
            skPoint(sketch, "E349.cCircle.centerSnap1", {"position": v(-651.96, 79) * mm});
            skLineSegment(sketch, "E349.2", {"start": v(-634.96, 70) * mm, "end": v(-643.96, 70) * mm});
            skLineSegment(sketch, "E349.3", {"start": v(-643.96, 70) * mm, "end": v(-643.96, 79) * mm});
            skPoint(sketch, "E349.0.midPoint", {"position": v(-634.96, 88) * mm});
            skPoint(sketch, "E350.orphan", {"position": v(-643.96, 88) * mm});
            skPoint(sketch, "E351.orphan", {"position": v(-625.96, 88) * mm});
            skPoint(sketch, "E352.orphan", {"position": v(-625.96, 70) * mm});
            skArc(sketch, "E353.cCircle", {"start": v(-415.37, -73.37) * mm, "mid": v(-421.74, -88.73) * mm, "end": v(-406.37, -82.37) * mm});
            skPoint(sketch, "E353.cCircle.centerSnap0", {"position": v(-415.37, -65.37) * mm});
            skPoint(sketch, "E353.cCircle.centerSnap1", {"position": v(-398.37, -82.37) * mm});
            skLineSegment(sketch, "E353.2", {"start": v(-415.37, -73.37) * mm, "end": v(-406.37, -73.37) * mm});
            skLineSegment(sketch, "E353.3", {"start": v(-406.37, -73.37) * mm, "end": v(-406.37, -82.37) * mm});
            skPoint(sketch, "E353.0.midPoint", {"position": v(-415.37, -91.37) * mm});
            skPoint(sketch, "E354.orphan", {"position": v(-424.37, -91.37) * mm});
            skPoint(sketch, "E355.orphan", {"position": v(-424.37, -73.37) * mm});
            skPoint(sketch, "E356.orphan", {"position": v(-406.37, -91.37) * mm});
            skArc(sketch, "E357.cCircle", {"start": v(-406.37, 71.63) * mm, "mid": v(-421.74, 78) * mm, "end": v(-415.37, 62.63) * mm});
            skPoint(sketch, "E357.cCircle.centerSnap0", {"position": v(-398.37, 71.63) * mm});
            skPoint(sketch, "E357.cCircle.centerSnap1", {"position": v(-415.37, 54.63) * mm});
            skLineSegment(sketch, "E357.0", {"start": v(-406.37, 62.63) * mm, "end": v(-415.37, 62.63) * mm});
            skLineSegment(sketch, "E357.3", {"start": v(-406.37, 71.63) * mm, "end": v(-406.37, 62.63) * mm});
            skPoint(sketch, "E357.0.midPoint", {"position": v(-415.37, 62.63) * mm});
            skPoint(sketch, "E358.orphan", {"position": v(-424.37, 80.63) * mm});
            skPoint(sketch, "E359.orphan", {"position": v(-424.37, 62.63) * mm});
            skPoint(sketch, "E360.orphan", {"position": v(-406.37, 80.63) * mm});
            skArc(sketch, "E361.cCircle", {"start": v(-311.37, 62.63) * mm, "mid": v(-305.01, 78) * mm, "end": v(-320.37, 71.63) * mm});
            skPoint(sketch, "E361.cCircle.centerSnap0", {"position": v(-311.37, 54.63) * mm});
            skPoint(sketch, "E361.cCircle.centerSnap1", {"position": v(-328.37, 71.63) * mm});
            skLineSegment(sketch, "E361.0", {"start": v(-311.37, 62.63) * mm, "end": v(-320.37, 62.63) * mm});
            skLineSegment(sketch, "E361.1", {"start": v(-320.37, 62.63) * mm, "end": v(-320.37, 71.63) * mm});
            skPoint(sketch, "E361.0.midPoint", {"position": v(-311.37, 62.63) * mm});
            skPoint(sketch, "E362.orphan", {"position": v(-320.37, 80.63) * mm});
            skPoint(sketch, "E363.orphan", {"position": v(-302.37, 80.63) * mm});
            skPoint(sketch, "E364.orphan", {"position": v(-302.37, 62.63) * mm});
            skCircle(sketch, "E365.cCircle", {"center": v(-311.37, -82.37) * mm, "radius": 9 * mm});
            skPoint(sketch, "E365.cCircle.centerSnap0", {"position": v(-311.37, -65.37) * mm});
            skPoint(sketch, "E365.cCircle.centerSnap1", {"position": v(-328.37, -82.37) * mm});
            skLineSegment(sketch, "E365.1", {"start": v(-320.37, -82.37) * mm, "end": v(-320.37, -73.37) * mm});
            skLineSegment(sketch, "E365.2", {"start": v(-320.37, -73.37) * mm, "end": v(-311.37, -73.37) * mm});
            skPoint(sketch, "E365.0.midPoint", {"position": v(-311.37, -91.37) * mm});
            skPoint(sketch, "E366.orphan", {"position": v(-302.37, -73.37) * mm});
            skPoint(sketch, "E367.orphan", {"position": v(-302.37, -91.37) * mm});
            skPoint(sketch, "E368.orphan", {"position": v(-320.37, -91.37) * mm});
            skArc(sketch, "E369.cCircle", {"start": v(-104.36, 73.55) * mm, "mid": v(-119.72, 79.92) * mm, "end": v(-113.36, 64.55) * mm});
            skPoint(sketch, "E369.cCircle.centerSnap0", {"position": v(-113.36, 56.55) * mm});
            skPoint(sketch, "E369.cCircle.centerSnap1", {"position": v(-96.36, 73.55) * mm});
            skLineSegment(sketch, "E369.0", {"start": v(-104.36, 64.55) * mm, "end": v(-113.36, 64.55) * mm});
            skLineSegment(sketch, "E369.3", {"start": v(-104.36, 73.55) * mm, "end": v(-104.36, 64.55) * mm});
            skPoint(sketch, "E369.0.midPoint", {"position": v(-113.36, 64.55) * mm});
            skPoint(sketch, "E370.orphan", {"position": v(-122.36, 82.55) * mm});
            skPoint(sketch, "E371.orphan", {"position": v(-122.36, 64.55) * mm});
            skPoint(sketch, "E372.orphan", {"position": v(-104.36, 82.55) * mm});
            skArc(sketch, "E373.cCircle", {"start": v(-113.36, -71.45) * mm, "mid": v(-119.72, -86.81) * mm, "end": v(-104.36, -80.45) * mm});
            skPoint(sketch, "E373.cCircle.centerSnap0", {"position": v(-96.36, -80.45) * mm});
            skPoint(sketch, "E373.cCircle.centerSnap1", {"position": v(-113.36, -63.45) * mm});
            skLineSegment(sketch, "E373.0", {"start": v(-113.36, -71.45) * mm, "end": v(-104.36, -71.45) * mm});
            skLineSegment(sketch, "E373.1", {"start": v(-104.36, -71.45) * mm, "end": v(-104.36, -80.45) * mm});
            skPoint(sketch, "E373.0.midPoint", {"position": v(-113.36, -71.45) * mm});
            skPoint(sketch, "E374.orphan", {"position": v(-122.36, -89.45) * mm});
            skPoint(sketch, "E375.orphan", {"position": v(-122.36, -71.45) * mm});
            skArc(sketch, "E376.cCircle", {"start": v(135.64, 71.49) * mm, "mid": v(120.28, 77.85) * mm, "end": v(126.64, 62.49) * mm});
            skPoint(sketch, "E376.cCircle.centerSnap0", {"position": v(126.64, 54.49) * mm});
            skPoint(sketch, "E376.cCircle.centerSnap1", {"position": v(143.64, 71.49) * mm});
            skLineSegment(sketch, "E376.0", {"start": v(135.64, 62.49) * mm, "end": v(126.64, 62.49) * mm});
            skLineSegment(sketch, "E376.3", {"start": v(135.64, 71.49) * mm, "end": v(135.64, 62.49) * mm});
            skPoint(sketch, "E376.0.midPoint", {"position": v(126.64, 62.49) * mm});
            skPoint(sketch, "E377.orphan", {"position": v(117.64, 80.49) * mm});
            skPoint(sketch, "E378.orphan", {"position": v(117.64, 62.49) * mm});
            skPoint(sketch, "E379.orphan", {"position": v(135.64, 80.49) * mm});
            skArc(sketch, "E380.cCircle", {"start": v(126.64, -73.51) * mm, "mid": v(120.28, -88.88) * mm, "end": v(135.64, -82.51) * mm});
            skPoint(sketch, "E380.cCircle.centerSnap0", {"position": v(126.64, -65.51) * mm});
            skPoint(sketch, "E380.cCircle.centerSnap1", {"position": v(143.64, -82.51) * mm});
            skLineSegment(sketch, "E380.0", {"start": v(126.64, -73.51) * mm, "end": v(135.64, -73.51) * mm});
            skLineSegment(sketch, "E380.1", {"start": v(135.64, -73.51) * mm, "end": v(135.64, -82.51) * mm});
            skPoint(sketch, "E380.0.midPoint", {"position": v(126.64, -73.51) * mm});
            skPoint(sketch, "E381.orphan", {"position": v(117.64, -91.51) * mm});
            skPoint(sketch, "E382.orphan", {"position": v(117.64, -73.51) * mm});
            skArc(sketch, "E383.cCircle", {"start": v(345.12, -73.4) * mm, "mid": v(338.76, -88.77) * mm, "end": v(354.12, -82.4) * mm});
            skPoint(sketch, "E383.cCircle.centerSnap0", {"position": v(362.12, -82.4) * mm});
            skPoint(sketch, "E383.cCircle.centerSnap1", {"position": v(345.12, -65.4) * mm});
            skLineSegment(sketch, "E383.0", {"start": v(345.12, -73.4) * mm, "end": v(354.12, -73.4) * mm});
            skLineSegment(sketch, "E383.1", {"start": v(354.12, -73.4) * mm, "end": v(354.12, -82.4) * mm});
            skPoint(sketch, "E383.0.midPoint", {"position": v(345.12, -73.4) * mm});
            skPoint(sketch, "E384.orphan", {"position": v(336.12, -73.4) * mm});
            skArc(sketch, "E385.cCircle", {"start": v(354.12, 71.6) * mm, "mid": v(338.76, 77.96) * mm, "end": v(345.12, 62.6) * mm});
            skPoint(sketch, "E385.cCircle.centerSnap0", {"position": v(345.12, 54.6) * mm});
            skPoint(sketch, "E385.cCircle.centerSnap1", {"position": v(362.12, 71.6) * mm});
            skLineSegment(sketch, "E385.0", {"start": v(354.12, 62.6) * mm, "end": v(345.12, 62.6) * mm});
            skLineSegment(sketch, "E385.3", {"start": v(354.12, 71.6) * mm, "end": v(354.12, 62.6) * mm});
            skPoint(sketch, "E385.0.midPoint", {"position": v(345.12, 62.6) * mm});
            skPoint(sketch, "E386.orphan", {"position": v(336.12, 80.6) * mm});
            skPoint(sketch, "E387.orphan", {"position": v(336.12, 62.6) * mm});
            skPoint(sketch, "E388.orphan", {"position": v(354.12, 80.6) * mm});
            skArc(sketch, "E389.cCircle", {"start": v(519.12, 62.6) * mm, "mid": v(525.49, 77.96) * mm, "end": v(510.12, 71.6) * mm});
            skPoint(sketch, "E389.cCircle.centerSnap0", {"position": v(519.12, 54.6) * mm});
            skPoint(sketch, "E389.cCircle.centerSnap1", {"position": v(502.12, 71.6) * mm});
            skLineSegment(sketch, "E389.0", {"start": v(519.12, 62.6) * mm, "end": v(510.12, 62.6) * mm});
            skLineSegment(sketch, "E389.1", {"start": v(510.12, 62.6) * mm, "end": v(510.12, 71.6) * mm});
            skPoint(sketch, "E389.0.midPoint", {"position": v(519.12, 62.6) * mm});
            skPoint(sketch, "E390.orphan", {"position": v(510.12, 80.6) * mm});
            skPoint(sketch, "E391.orphan", {"position": v(528.12, 80.6) * mm});
            skPoint(sketch, "E392.orphan", {"position": v(528.12, 62.6) * mm});
            skArc(sketch, "E393.cCircle", {"start": v(510.12, -82.4) * mm, "mid": v(525.49, -88.77) * mm, "end": v(519.12, -73.4) * mm});
            skPoint(sketch, "E393.cCircle.centerSnap0", {"position": v(502.12, -82.4) * mm});
            skPoint(sketch, "E393.cCircle.centerSnap1", {"position": v(519.12, -65.4) * mm});
            skLineSegment(sketch, "E393.0", {"start": v(510.12, -73.4) * mm, "end": v(519.12, -73.4) * mm});
            skLineSegment(sketch, "E393.3", {"start": v(510.12, -82.4) * mm, "end": v(510.12, -73.4) * mm});
            skPoint(sketch, "E393.0.midPoint", {"position": v(519.12, -73.4) * mm});
            skPoint(sketch, "E394.orphan", {"position": v(510.12, -91.4) * mm});
            skPoint(sketch, "E395.orphan", {"position": v(528.12, -73.4) * mm});
            skArc(sketch, "E396.cCircle", {"start": v(683.08, -74.6) * mm, "mid": v(676.72, -89.97) * mm, "end": v(692.08, -83.6) * mm});
            skPoint(sketch, "E396.cCircle.centerSnap0", {"position": v(700.08, -83.6) * mm});
            skPoint(sketch, "E396.cCircle.centerSnap1", {"position": v(683.08, -66.6) * mm});
            skLineSegment(sketch, "E396.0", {"start": v(683.08, -74.6) * mm, "end": v(692.08, -74.6) * mm});
            skLineSegment(sketch, "E396.1", {"start": v(692.08, -74.6) * mm, "end": v(692.08, -83.6) * mm});
            skPoint(sketch, "E396.0.midPoint", {"position": v(683.08, -74.6) * mm});
            skPoint(sketch, "E397.orphan", {"position": v(674.08, -92.6) * mm});
            skPoint(sketch, "E398.orphan", {"position": v(674.08, -74.6) * mm});
            skArc(sketch, "E399.cCircle", {"start": v(878.08, -83.6) * mm, "mid": v(893.45, -89.97) * mm, "end": v(887.08, -74.6) * mm});
            skPoint(sketch, "E399.cCircle.centerSnap0", {"position": v(887.08, -66.6) * mm});
            skPoint(sketch, "E399.cCircle.centerSnap1", {"position": v(870.08, -83.6) * mm});
            skLineSegment(sketch, "E399.0", {"start": v(878.08, -74.6) * mm, "end": v(887.08, -74.6) * mm});
            skLineSegment(sketch, "E399.3", {"start": v(878.08, -83.6) * mm, "end": v(878.08, -74.6) * mm});
            skPoint(sketch, "E399.0.midPoint", {"position": v(887.08, -74.6) * mm});
            skPoint(sketch, "E400.orphan", {"position": v(896.08, -74.6) * mm});
            skPoint(sketch, "E401.orphan", {"position": v(896.08, -92.6) * mm});
            skPoint(sketch, "E402.orphan", {"position": v(878.08, -92.6) * mm});
            skArc(sketch, "E403.cCircle", {"start": v(887.08, 61.4) * mm, "mid": v(893.45, 76.76) * mm, "end": v(878.08, 70.4) * mm});
            skPoint(sketch, "E403.cCircle.centerSnap0", {"position": v(887.08, 53.4) * mm});
            skPoint(sketch, "E403.cCircle.centerSnap1", {"position": v(870.08, 70.4) * mm});
            skLineSegment(sketch, "E403.0", {"start": v(887.08, 61.4) * mm, "end": v(878.08, 61.4) * mm});
            skLineSegment(sketch, "E403.1", {"start": v(878.08, 61.4) * mm, "end": v(878.08, 70.4) * mm});
            skPoint(sketch, "E403.0.midPoint", {"position": v(887.08, 61.4) * mm});
            skPoint(sketch, "E404.orphan", {"position": v(878.08, 79.4) * mm});
            skPoint(sketch, "E405.orphan", {"position": v(896.08, 79.4) * mm});
            skPoint(sketch, "E406.orphan", {"position": v(896.08, 61.4) * mm});
            skArc(sketch, "E407.cCircle", {"start": v(692.08, 70.4) * mm, "mid": v(676.72, 76.76) * mm, "end": v(683.08, 61.4) * mm});
            skPoint(sketch, "E407.cCircle.centerSnap0", {"position": v(683.08, 53.4) * mm});
            skPoint(sketch, "E407.cCircle.centerSnap1", {"position": v(700.08, 70.4) * mm});
            skLineSegment(sketch, "E407.0", {"start": v(692.08, 61.4) * mm, "end": v(683.08, 61.4) * mm});
            skLineSegment(sketch, "E407.3", {"start": v(692.08, 70.4) * mm, "end": v(692.08, 61.4) * mm});
            skPoint(sketch, "E407.0.midPoint", {"position": v(683.08, 61.4) * mm});
            skPoint(sketch, "E408.orphan", {"position": v(674.08, 79.4) * mm});
            skPoint(sketch, "E409.orphan", {"position": v(674.08, 61.4) * mm});
            skPoint(sketch, "E410.orphan", {"position": v(692.08, 79.4) * mm});
            skSolve(sketch);
        }
        {
            var Q0;
            Q0 = qSketchRegion(id + "F0", true);
            extrude(context, id + "F1", {"entities" : qUnion([Q0]), "depth" : 190 * mm});
        }
        {
            var Q0;
            Q0=qCreatedBy(makeId("Top.planeOp"),FACE);
            var sketch = newSketch(context, id + "F2", { "sketchPlane" : qUnion([Q0])});
            skLineSegment(sketch, "E411", {"start": v(-910.8, -201.78) * mm, "end": v(-910.8, -391.78) * mm});
            skLineSegment(sketch, "E412", {"start": v(-910.8, -391.78) * mm, "end": v(-620.8, -391.78) * mm});
            skLineSegment(sketch, "E413", {"start": v(-620.8, -391.78) * mm, "end": v(-620.8, -201.78) * mm});
            skLineSegment(sketch, "E414", {"start": v(-620.8, -201.78) * mm, "end": v(-910.8, -201.78) * mm});
            skLineSegment(sketch, "E415", {"start": v(-875.8, -210.78) * mm, "end": v(-875.8, -228.78) * mm});
            skLineSegment(sketch, "E416", {"start": v(-875.8, -228.78) * mm, "end": v(-845.8, -228.78) * mm});
            skLineSegment(sketch, "E417", {"start": v(-845.8, -228.78) * mm, "end": v(-845.8, -210.78) * mm});
            skLineSegment(sketch, "E418", {"start": v(-845.8, -210.78) * mm, "end": v(-875.8, -210.78) * mm});
            skLineSegment(sketch, "E419", {"start": v(-837.8, -210.78) * mm, "end": v(-837.8, -228.78) * mm});
            skLineSegment(sketch, "E420", {"start": v(-837.8, -228.78) * mm, "end": v(-807.8, -228.78) * mm});
            skLineSegment(sketch, "E421", {"start": v(-807.8, -228.78) * mm, "end": v(-807.8, -210.78) * mm});
            skLineSegment(sketch, "E422", {"start": v(-807.8, -210.78) * mm, "end": v(-837.8, -210.78) * mm});
            skLineSegment(sketch, "E423", {"start": v(-799.8, -210.78) * mm, "end": v(-799.8, -228.78) * mm});
            skLineSegment(sketch, "E424", {"start": v(-799.8, -228.78) * mm, "end": v(-769.8, -228.78) * mm});
            skLineSegment(sketch, "E425", {"start": v(-769.8, -228.78) * mm, "end": v(-769.8, -210.78) * mm});
            skLineSegment(sketch, "E426", {"start": v(-769.8, -210.78) * mm, "end": v(-799.8, -210.78) * mm});
            skLineSegment(sketch, "E427", {"start": v(-761.8, -210.78) * mm, "end": v(-761.8, -228.78) * mm});
            skLineSegment(sketch, "E428", {"start": v(-761.8, -228.78) * mm, "end": v(-731.8, -228.78) * mm});
            skLineSegment(sketch, "E429", {"start": v(-731.8, -228.78) * mm, "end": v(-731.8, -210.78) * mm});
            skLineSegment(sketch, "E430", {"start": v(-731.8, -210.78) * mm, "end": v(-761.8, -210.78) * mm});
            skLineSegment(sketch, "E431", {"start": v(-723.8, -210.78) * mm, "end": v(-723.8, -228.78) * mm});
            skLineSegment(sketch, "E432", {"start": v(-723.8, -228.78) * mm, "end": v(-693.8, -228.78) * mm});
            skLineSegment(sketch, "E433", {"start": v(-693.8, -228.78) * mm, "end": v(-693.8, -210.78) * mm});
            skLineSegment(sketch, "E434", {"start": v(-693.8, -210.78) * mm, "end": v(-723.8, -210.78) * mm});
            skLineSegment(sketch, "E435", {"start": v(-685.8, -210.78) * mm, "end": v(-685.8, -228.78) * mm});
            skLineSegment(sketch, "E436", {"start": v(-685.8, -228.78) * mm, "end": v(-655.8, -228.78) * mm});
            skLineSegment(sketch, "E437", {"start": v(-655.8, -228.78) * mm, "end": v(-655.8, -210.78) * mm});
            skLineSegment(sketch, "E438", {"start": v(-655.8, -210.78) * mm, "end": v(-685.8, -210.78) * mm});
            skLineSegment(sketch, "E439", {"start": v(-647.8, -236.78) * mm, "end": v(-647.8, -271.44) * mm});
            skLineSegment(sketch, "E440", {"start": v(-647.8, -271.44) * mm, "end": v(-629.8, -271.44) * mm});
            skLineSegment(sketch, "E441", {"start": v(-629.8, -271.44) * mm, "end": v(-629.8, -236.78) * mm});
            skLineSegment(sketch, "E442", {"start": v(-629.8, -236.78) * mm, "end": v(-647.8, -236.78) * mm});
            skLineSegment(sketch, "E443", {"start": v(-901.8, -236.78) * mm, "end": v(-901.8, -271.44) * mm});
            skLineSegment(sketch, "E444", {"start": v(-901.8, -271.44) * mm, "end": v(-883.8, -271.44) * mm});
            skLineSegment(sketch, "E445", {"start": v(-883.8, -271.44) * mm, "end": v(-883.8, -236.78) * mm});
            skLineSegment(sketch, "E446", {"start": v(-883.8, -236.78) * mm, "end": v(-901.8, -236.78) * mm});
            skLineSegment(sketch, "E447", {"start": v(-901.8, -279.44) * mm, "end": v(-901.8, -314.1) * mm});
            skLineSegment(sketch, "E448", {"start": v(-901.8, -314.1) * mm, "end": v(-883.8, -314.1) * mm});
            skLineSegment(sketch, "E449", {"start": v(-883.8, -314.1) * mm, "end": v(-883.8, -279.44) * mm});
            skLineSegment(sketch, "E450", {"start": v(-883.8, -279.44) * mm, "end": v(-901.8, -279.44) * mm});
            skLineSegment(sketch, "E451", {"start": v(-901.8, -322.1) * mm, "end": v(-901.8, -356.78) * mm});
            skLineSegment(sketch, "E452", {"start": v(-901.8, -356.78) * mm, "end": v(-883.8, -356.78) * mm});
            skLineSegment(sketch, "E453", {"start": v(-883.8, -356.78) * mm, "end": v(-883.8, -322.1) * mm});
            skLineSegment(sketch, "E454", {"start": v(-883.8, -322.1) * mm, "end": v(-901.8, -322.1) * mm});
            skLineSegment(sketch, "E455", {"start": v(-875.8, -364.78) * mm, "end": v(-875.8, -382.78) * mm});
            skLineSegment(sketch, "E456", {"start": v(-875.8, -382.78) * mm, "end": v(-845.8, -382.78) * mm});
            skLineSegment(sketch, "E457", {"start": v(-845.8, -382.78) * mm, "end": v(-845.8, -364.78) * mm});
            skLineSegment(sketch, "E458", {"start": v(-845.8, -364.78) * mm, "end": v(-875.8, -364.78) * mm});
            skLineSegment(sketch, "E459", {"start": v(-837.8, -364.78) * mm, "end": v(-837.8, -382.78) * mm});
            skLineSegment(sketch, "E460", {"start": v(-837.8, -382.78) * mm, "end": v(-807.8, -382.78) * mm});
            skLineSegment(sketch, "E461", {"start": v(-807.8, -382.78) * mm, "end": v(-807.8, -364.78) * mm});
            skLineSegment(sketch, "E462", {"start": v(-807.8, -364.78) * mm, "end": v(-837.8, -364.78) * mm});
            skLineSegment(sketch, "E463", {"start": v(-875.8, -236.78) * mm, "end": v(-875.8, -356.78) * mm});
            skLineSegment(sketch, "E464", {"start": v(-875.8, -356.78) * mm, "end": v(-793.3, -356.78) * mm});
            skLineSegment(sketch, "E465", {"start": v(-793.3, -356.78) * mm, "end": v(-793.3, -236.78) * mm});
            skLineSegment(sketch, "E466", {"start": v(-793.3, -236.78) * mm, "end": v(-875.8, -236.78) * mm});
            skLineSegment(sketch, "E467", {"start": v(-799.8, -364.78) * mm, "end": v(-799.8, -382.78) * mm});
            skLineSegment(sketch, "E468", {"start": v(-799.8, -382.78) * mm, "end": v(-769.8, -382.78) * mm});
            skLineSegment(sketch, "E469", {"start": v(-769.8, -382.78) * mm, "end": v(-769.8, -364.78) * mm});
            skLineSegment(sketch, "E470", {"start": v(-769.8, -364.78) * mm, "end": v(-799.8, -364.78) * mm});
            skLineSegment(sketch, "E471", {"start": v(-761.8, -364.78) * mm, "end": v(-761.8, -382.78) * mm});
            skLineSegment(sketch, "E472", {"start": v(-761.8, -382.78) * mm, "end": v(-731.8, -382.78) * mm});
            skLineSegment(sketch, "E473", {"start": v(-731.8, -382.78) * mm, "end": v(-731.8, -364.78) * mm});
            skLineSegment(sketch, "E474", {"start": v(-731.8, -364.78) * mm, "end": v(-761.8, -364.78) * mm});
            skLineSegment(sketch, "E475", {"start": v(-723.8, -364.78) * mm, "end": v(-723.8, -382.78) * mm});
            skLineSegment(sketch, "E476", {"start": v(-723.8, -382.78) * mm, "end": v(-693.8, -382.78) * mm});
            skLineSegment(sketch, "E477", {"start": v(-693.8, -382.78) * mm, "end": v(-693.8, -364.78) * mm});
            skLineSegment(sketch, "E478", {"start": v(-693.8, -364.78) * mm, "end": v(-723.8, -364.78) * mm});
            skLineSegment(sketch, "E479", {"start": v(-685.8, -364.78) * mm, "end": v(-685.8, -382.78) * mm});
            skLineSegment(sketch, "E480", {"start": v(-685.8, -382.78) * mm, "end": v(-655.8, -382.78) * mm});
            skLineSegment(sketch, "E481", {"start": v(-655.8, -382.78) * mm, "end": v(-655.8, -364.78) * mm});
            skLineSegment(sketch, "E482", {"start": v(-655.8, -364.78) * mm, "end": v(-685.8, -364.78) * mm});
            skLineSegment(sketch, "E483", {"start": v(-647.8, -356.78) * mm, "end": v(-647.8, -322.1) * mm});
            skLineSegment(sketch, "E484", {"start": v(-647.8, -322.1) * mm, "end": v(-629.8, -322.1) * mm});
            skLineSegment(sketch, "E485", {"start": v(-629.8, -322.1) * mm, "end": v(-629.8, -356.78) * mm});
            skLineSegment(sketch, "E486", {"start": v(-629.8, -356.78) * mm, "end": v(-647.8, -356.78) * mm});
            skLineSegment(sketch, "E487", {"start": v(-629.8, -314.1) * mm, "end": v(-629.8, -279.44) * mm});
            skLineSegment(sketch, "E488", {"start": v(-629.8, -279.44) * mm, "end": v(-647.8, -279.44) * mm});
            skLineSegment(sketch, "E489", {"start": v(-647.8, -279.44) * mm, "end": v(-647.8, -314.1) * mm});
            skLineSegment(sketch, "E490", {"start": v(-647.8, -314.1) * mm, "end": v(-629.8, -314.1) * mm});
            skLineSegment(sketch, "E491", {"start": v(-738.3, -236.78) * mm, "end": v(-738.3, -356.78) * mm});
            skLineSegment(sketch, "E492", {"start": v(-738.3, -356.78) * mm, "end": v(-655.8, -356.78) * mm});
            skLineSegment(sketch, "E493", {"start": v(-655.8, -356.78) * mm, "end": v(-655.8, -236.78) * mm});
            skLineSegment(sketch, "E494", {"start": v(-655.8, -236.78) * mm, "end": v(-738.3, -236.78) * mm});
            skLineSegment(sketch, "E495", {"start": v(-746.3, -356.78) * mm, "end": v(-746.3, -304.78) * mm});
            skLineSegment(sketch, "E496", {"start": v(-746.3, -304.78) * mm, "end": v(-785.3, -304.78) * mm});
            skLineSegment(sketch, "E497", {"start": v(-785.3, -304.78) * mm, "end": v(-785.3, -356.78) * mm});
            skLineSegment(sketch, "E498", {"start": v(-785.3, -356.78) * mm, "end": v(-746.3, -356.78) * mm});
            skLineSegment(sketch, "E499", {"start": v(-785.3, -236.78) * mm, "end": v(-785.3, -296.78) * mm});
            skLineSegment(sketch, "E500", {"start": v(-785.3, -296.78) * mm, "end": v(-746.3, -296.78) * mm});
            skLineSegment(sketch, "E501", {"start": v(-746.3, -296.78) * mm, "end": v(-746.3, -236.78) * mm});
            skLineSegment(sketch, "E502", {"start": v(-746.3, -236.78) * mm, "end": v(-785.3, -236.78) * mm});
            skArc(sketch, "E503.cCircle", {"start": v(-883.8, -219.78) * mm, "mid": v(-899.16, -213.41) * mm, "end": v(-892.8, -228.78) * mm});
            skPoint(sketch, "E503.cCircle.centerSnap0", {"position": v(-892.8, -236.78) * mm});
            skPoint(sketch, "E503.cCircle.centerSnap1", {"position": v(-875.8, -219.78) * mm});
            skLineSegment(sketch, "E503.1", {"start": v(-883.8, -219.78) * mm, "end": v(-883.8, -228.78) * mm});
            skLineSegment(sketch, "E503.2", {"start": v(-883.8, -228.78) * mm, "end": v(-892.8, -228.78) * mm});
            skPoint(sketch, "E503.0.midPoint", {"position": v(-892.8, -210.78) * mm});
            skPoint(sketch, "E504.orphan", {"position": v(-901.8, -210.78) * mm});
            skPoint(sketch, "E503.0.end.orphan", {"position": v(-883.8, -210.78) * mm});
            skArc(sketch, "E505.cCircle", {"start": v(-892.8, -364.78) * mm, "mid": v(-899.16, -380.14) * mm, "end": v(-883.8, -373.78) * mm});
            skPoint(sketch, "E505.cCircle.centerSnap0", {"position": v(-875.8, -373.78) * mm});
            skPoint(sketch, "E505.cCircle.centerSnap1", {"position": v(-892.8, -356.78) * mm});
            skLineSegment(sketch, "E505.2", {"start": v(-892.8, -364.78) * mm, "end": v(-883.8, -364.78) * mm});
            skLineSegment(sketch, "E505.3", {"start": v(-883.8, -364.78) * mm, "end": v(-883.8, -373.78) * mm});
            skPoint(sketch, "E505.0.midPoint", {"position": v(-892.8, -382.78) * mm});
            skPoint(sketch, "E506.orphan", {"position": v(-901.8, -364.78) * mm});
            skPoint(sketch, "E507.orphan", {"position": v(-901.8, -382.78) * mm});
            skPoint(sketch, "E508.orphan", {"position": v(-883.8, -382.78) * mm});
            skArc(sketch, "E509.cCircle", {"start": v(-647.8, -373.78) * mm, "mid": v(-632.44, -380.14) * mm, "end": v(-638.8, -364.78) * mm});
            skPoint(sketch, "E509.cCircle.centerSnap0", {"position": v(-638.8, -356.78) * mm});
            skPoint(sketch, "E509.cCircle.centerSnap1", {"position": v(-655.8, -373.78) * mm});
            skLineSegment(sketch, "E509.1", {"start": v(-647.8, -373.78) * mm, "end": v(-647.8, -364.78) * mm});
            skLineSegment(sketch, "E509.2", {"start": v(-647.8, -364.78) * mm, "end": v(-638.8, -364.78) * mm});
            skPoint(sketch, "E509.0.midPoint", {"position": v(-638.8, -382.78) * mm});
            skPoint(sketch, "E510.orphan", {"position": v(-647.8, -382.78) * mm});
            skPoint(sketch, "E511.orphan", {"position": v(-629.8, -382.78) * mm});
            skArc(sketch, "E512.cCircle", {"start": v(-638.8, -228.78) * mm, "mid": v(-632.44, -213.41) * mm, "end": v(-647.8, -219.78) * mm});
            skPoint(sketch, "E512.cCircle.centerSnap0", {"position": v(-638.8, -236.78) * mm});
            skPoint(sketch, "E512.cCircle.centerSnap1", {"position": v(-655.8, -219.78) * mm});
            skLineSegment(sketch, "E512.2", {"start": v(-638.8, -228.78) * mm, "end": v(-647.8, -228.78) * mm});
            skLineSegment(sketch, "E512.3", {"start": v(-647.8, -228.78) * mm, "end": v(-647.8, -219.78) * mm});
            skPoint(sketch, "E512.0.midPoint", {"position": v(-638.8, -210.78) * mm});
            skPoint(sketch, "E513.orphan", {"position": v(-647.8, -210.78) * mm});
            skPoint(sketch, "E514.orphan", {"position": v(-629.8, -210.78) * mm});
            skPoint(sketch, "E515.orphan", {"position": v(-629.8, -228.78) * mm});
            skSolve(sketch);
        }
        {
            var Q0;
            Q0 = qSketchRegion(id + "F2", true);
            extrude(context, id + "F3", {"entities" : qUnion([Q0]), "depth" : 90 * mm});
        }
        {
            var Q0;
            Q0=makeQuery(id+"F1.opExtrude","SWEPT_BODY",BODY,{"disambiguationData":[OSD([sQuery(id+"F0.wireOp",EDGE,"E0"),sQuery(id+"F0.wireOp",EDGE,"E1"),sQuery(id+"F0.wireOp",EDGE,"E2"),sQuery(id+"F0.wireOp",EDGE,"E3"),sQuery(id+"F0.wireOp",EDGE,"E4"),sQuery(id+"F0.wireOp",EDGE,"E5"),sQuery(id+"F0.wireOp",EDGE,"E6"),sQuery(id+"F0.wireOp",EDGE,"E7"),sQuery(id+"F0.wireOp",EDGE,"E8"),sQuery(id+"F0.wireOp",EDGE,"E9"),sQuery(id+"F0.wireOp",EDGE,"E10"),sQuery(id+"F0.wireOp",EDGE,"E11"),sQuery(id+"F0.wireOp",EDGE,"E12"),sQuery(id+"F0.wireOp",EDGE,"E13"),sQuery(id+"F0.wireOp",EDGE,"E14"),sQuery(id+"F0.wireOp",EDGE,"E15"),sQuery(id+"F0.wireOp",EDGE,"E16"),sQuery(id+"F0.wireOp",EDGE,"E17"),sQuery(id+"F0.wireOp",EDGE,"E18"),sQuery(id+"F0.wireOp",EDGE,"E19"),sQuery(id+"F0.wireOp",EDGE,"E20"),sQuery(id+"F0.wireOp",EDGE,"E21"),sQuery(id+"F0.wireOp",EDGE,"E22"),sQuery(id+"F0.wireOp",EDGE,"E23"),sQuery(id+"F0.wireOp",EDGE,"E24"),sQuery(id+"F0.wireOp",EDGE,"E25"),sQuery(id+"F0.wireOp",EDGE,"E26"),sQuery(id+"F0.wireOp",EDGE,"E27"),sQuery(id+"F0.wireOp",EDGE,"E28"),sQuery(id+"F0.wireOp",EDGE,"E29"),sQuery(id+"F0.wireOp",EDGE,"E30"),sQuery(id+"F0.wireOp",EDGE,"E31"),sQuery(id+"F0.wireOp",EDGE,"E32"),sQuery(id+"F0.wireOp",EDGE,"E33"),sQuery(id+"F0.wireOp",EDGE,"E34"),sQuery(id+"F0.wireOp",EDGE,"E35"),sQuery(id+"F0.wireOp",EDGE,"E36"),sQuery(id+"F0.wireOp",EDGE,"E37"),sQuery(id+"F0.wireOp",EDGE,"E38"),sQuery(id+"F0.wireOp",EDGE,"E39"),sQuery(id+"F0.wireOp",EDGE,"E40"),sQuery(id+"F0.wireOp",EDGE,"E41"),sQuery(id+"F0.wireOp",EDGE,"E42"),sQuery(id+"F0.wireOp",EDGE,"E43"),sQuery(id+"F0.wireOp",EDGE,"E44"),sQuery(id+"F0.wireOp",EDGE,"E45"),sQuery(id+"F0.wireOp",EDGE,"E46"),sQuery(id+"F0.wireOp",EDGE,"E47"),sQuery(id+"F0.wireOp",EDGE,"E48"),sQuery(id+"F0.wireOp",EDGE,"E49"),sQuery(id+"F0.wireOp",EDGE,"E50"),sQuery(id+"F0.wireOp",EDGE,"E51"),sQuery(id+"F0.wireOp",EDGE,"E52"),sQuery(id+"F0.wireOp",EDGE,"E53"),sQuery(id+"F0.wireOp",EDGE,"E54"),sQuery(id+"F0.wireOp",EDGE,"E55"),sQuery(id+"F0.wireOp",EDGE,"E56"),sQuery(id+"F0.wireOp",EDGE,"E57"),sQuery(id+"F0.wireOp",EDGE,"E58"),sQuery(id+"F0.wireOp",EDGE,"E59"),sQuery(id+"F0.wireOp",EDGE,"E60"),sQuery(id+"F0.wireOp",EDGE,"E61"),sQuery(id+"F0.wireOp",EDGE,"E62"),sQuery(id+"F0.wireOp",EDGE,"E63"),sQuery(id+"F0.wireOp",EDGE,"E64"),sQuery(id+"F0.wireOp",EDGE,"E65"),sQuery(id+"F0.wireOp",EDGE,"E66"),sQuery(id+"F0.wireOp",EDGE,"E67"),sQuery(id+"F0.wireOp",EDGE,"E68"),sQuery(id+"F0.wireOp",EDGE,"E69"),sQuery(id+"F0.wireOp",EDGE,"E70"),sQuery(id+"F0.wireOp",EDGE,"E71"),sQuery(id+"F0.wireOp",EDGE,"E72"),sQuery(id+"F0.wireOp",EDGE,"E73"),sQuery(id+"F0.wireOp",EDGE,"E74"),sQuery(id+"F0.wireOp",EDGE,"E75"),sQuery(id+"F0.wireOp",EDGE,"E76"),sQuery(id+"F0.wireOp",EDGE,"E77"),sQuery(id+"F0.wireOp",EDGE,"E78"),sQuery(id+"F0.wireOp",EDGE,"E79"),sQuery(id+"F0.wireOp",EDGE,"E80"),sQuery(id+"F0.wireOp",EDGE,"E81"),sQuery(id+"F0.wireOp",EDGE,"E82"),sQuery(id+"F0.wireOp",EDGE,"E83"),sQuery(id+"F0.wireOp",EDGE,"E84"),sQuery(id+"F0.wireOp",EDGE,"E85"),sQuery(id+"F0.wireOp",EDGE,"E86"),sQuery(id+"F0.wireOp",EDGE,"E87"),sQuery(id+"F0.wireOp",EDGE,"E88"),sQuery(id+"F0.wireOp",EDGE,"E89"),sQuery(id+"F0.wireOp",EDGE,"E90"),sQuery(id+"F0.wireOp",EDGE,"E91"),sQuery(id+"F0.wireOp",EDGE,"E340.cCircle"),sQuery(id+"F0.wireOp",EDGE,"E340.1"),sQuery(id+"F0.wireOp",EDGE,"E340.2"),sQuery(id+"F0.wireOp",EDGE,"E342.cCircle"),sQuery(id+"F0.wireOp",EDGE,"E342.2"),sQuery(id+"F0.wireOp",EDGE,"E342.3"),sQuery(id+"F0.wireOp",EDGE,"E346.cCircle"),sQuery(id+"F0.wireOp",EDGE,"E346.1"),sQuery(id+"F0.wireOp",EDGE,"E346.2"),sQuery(id+"F0.wireOp",EDGE,"E349.cCircle"),sQuery(id+"F0.wireOp",EDGE,"E349.2"),sQuery(id+"F0.wireOp",EDGE,"E349.3")])]});
            transform(context, id + "F4", {"entities" : qUnion([Q0]), "transformType" : TransformType.TRANSLATION_3D, "dx" : 410 * mm, "dy" : -299 * mm, "dz" : 0 * mm, "makeCopy" : true});
        }
        {
            var Q0;
            Q0=makeQuery(id+"F4.opPattern","COPY",BODY,{"derivedFrom":makeQuery(id+"F1.opExtrude","SWEPT_BODY",BODY,{"disambiguationData":[OSD([sQuery(id+"F0.wireOp",EDGE,"E0"),sQuery(id+"F0.wireOp",EDGE,"E1"),sQuery(id+"F0.wireOp",EDGE,"E2"),sQuery(id+"F0.wireOp",EDGE,"E3"),sQuery(id+"F0.wireOp",EDGE,"E4"),sQuery(id+"F0.wireOp",EDGE,"E5"),sQuery(id+"F0.wireOp",EDGE,"E6"),sQuery(id+"F0.wireOp",EDGE,"E7"),sQuery(id+"F0.wireOp",EDGE,"E8"),sQuery(id+"F0.wireOp",EDGE,"E9"),sQuery(id+"F0.wireOp",EDGE,"E10"),sQuery(id+"F0.wireOp",EDGE,"E11"),sQuery(id+"F0.wireOp",EDGE,"E12"),sQuery(id+"F0.wireOp",EDGE,"E13"),sQuery(id+"F0.wireOp",EDGE,"E14"),sQuery(id+"F0.wireOp",EDGE,"E15"),sQuery(id+"F0.wireOp",EDGE,"E16"),sQuery(id+"F0.wireOp",EDGE,"E17"),sQuery(id+"F0.wireOp",EDGE,"E18"),sQuery(id+"F0.wireOp",EDGE,"E19"),sQuery(id+"F0.wireOp",EDGE,"E20"),sQuery(id+"F0.wireOp",EDGE,"E21"),sQuery(id+"F0.wireOp",EDGE,"E22"),sQuery(id+"F0.wireOp",EDGE,"E23"),sQuery(id+"F0.wireOp",EDGE,"E24"),sQuery(id+"F0.wireOp",EDGE,"E25"),sQuery(id+"F0.wireOp",EDGE,"E26"),sQuery(id+"F0.wireOp",EDGE,"E27"),sQuery(id+"F0.wireOp",EDGE,"E28"),sQuery(id+"F0.wireOp",EDGE,"E29"),sQuery(id+"F0.wireOp",EDGE,"E30"),sQuery(id+"F0.wireOp",EDGE,"E31"),sQuery(id+"F0.wireOp",EDGE,"E32"),sQuery(id+"F0.wireOp",EDGE,"E33"),sQuery(id+"F0.wireOp",EDGE,"E34"),sQuery(id+"F0.wireOp",EDGE,"E35"),sQuery(id+"F0.wireOp",EDGE,"E36"),sQuery(id+"F0.wireOp",EDGE,"E37"),sQuery(id+"F0.wireOp",EDGE,"E38"),sQuery(id+"F0.wireOp",EDGE,"E39"),sQuery(id+"F0.wireOp",EDGE,"E40"),sQuery(id+"F0.wireOp",EDGE,"E41"),sQuery(id+"F0.wireOp",EDGE,"E42"),sQuery(id+"F0.wireOp",EDGE,"E43"),sQuery(id+"F0.wireOp",EDGE,"E44"),sQuery(id+"F0.wireOp",EDGE,"E45"),sQuery(id+"F0.wireOp",EDGE,"E46"),sQuery(id+"F0.wireOp",EDGE,"E47"),sQuery(id+"F0.wireOp",EDGE,"E48"),sQuery(id+"F0.wireOp",EDGE,"E49"),sQuery(id+"F0.wireOp",EDGE,"E50"),sQuery(id+"F0.wireOp",EDGE,"E51"),sQuery(id+"F0.wireOp",EDGE,"E52"),sQuery(id+"F0.wireOp",EDGE,"E53"),sQuery(id+"F0.wireOp",EDGE,"E54"),sQuery(id+"F0.wireOp",EDGE,"E55"),sQuery(id+"F0.wireOp",EDGE,"E56"),sQuery(id+"F0.wireOp",EDGE,"E57"),sQuery(id+"F0.wireOp",EDGE,"E58"),sQuery(id+"F0.wireOp",EDGE,"E59"),sQuery(id+"F0.wireOp",EDGE,"E60"),sQuery(id+"F0.wireOp",EDGE,"E61"),sQuery(id+"F0.wireOp",EDGE,"E62"),sQuery(id+"F0.wireOp",EDGE,"E63"),sQuery(id+"F0.wireOp",EDGE,"E64"),sQuery(id+"F0.wireOp",EDGE,"E65"),sQuery(id+"F0.wireOp",EDGE,"E66"),sQuery(id+"F0.wireOp",EDGE,"E67"),sQuery(id+"F0.wireOp",EDGE,"E68"),sQuery(id+"F0.wireOp",EDGE,"E69"),sQuery(id+"F0.wireOp",EDGE,"E70"),sQuery(id+"F0.wireOp",EDGE,"E71"),sQuery(id+"F0.wireOp",EDGE,"E72"),sQuery(id+"F0.wireOp",EDGE,"E73"),sQuery(id+"F0.wireOp",EDGE,"E74"),sQuery(id+"F0.wireOp",EDGE,"E75"),sQuery(id+"F0.wireOp",EDGE,"E76"),sQuery(id+"F0.wireOp",EDGE,"E77"),sQuery(id+"F0.wireOp",EDGE,"E78"),sQuery(id+"F0.wireOp",EDGE,"E79"),sQuery(id+"F0.wireOp",EDGE,"E80"),sQuery(id+"F0.wireOp",EDGE,"E81"),sQuery(id+"F0.wireOp",EDGE,"E82"),sQuery(id+"F0.wireOp",EDGE,"E83"),sQuery(id+"F0.wireOp",EDGE,"E84"),sQuery(id+"F0.wireOp",EDGE,"E85"),sQuery(id+"F0.wireOp",EDGE,"E86"),sQuery(id+"F0.wireOp",EDGE,"E87"),sQuery(id+"F0.wireOp",EDGE,"E88"),sQuery(id+"F0.wireOp",EDGE,"E89"),sQuery(id+"F0.wireOp",EDGE,"E90"),sQuery(id+"F0.wireOp",EDGE,"E91"),sQuery(id+"F0.wireOp",EDGE,"E340.cCircle"),sQuery(id+"F0.wireOp",EDGE,"E340.1"),sQuery(id+"F0.wireOp",EDGE,"E340.2"),sQuery(id+"F0.wireOp",EDGE,"E342.cCircle"),sQuery(id+"F0.wireOp",EDGE,"E342.2"),sQuery(id+"F0.wireOp",EDGE,"E342.3"),sQuery(id+"F0.wireOp",EDGE,"E346.cCircle"),sQuery(id+"F0.wireOp",EDGE,"E346.1"),sQuery(id+"F0.wireOp",EDGE,"E346.2"),sQuery(id+"F0.wireOp",EDGE,"E349.cCircle"),sQuery(id+"F0.wireOp",EDGE,"E349.2"),sQuery(id+"F0.wireOp",EDGE,"E349.3")])]}),"instanceName":"1"});
            transform(context, id + "F5", {"entities" : qUnion([Q0]), "transformType" : TransformType.TRANSLATION_3D, "dx" : 374 * mm, "dy" : 0 * mm, "dz" : 0 * mm, "makeCopy" : true});
        }
        {
            var Q0;
            Q0=makeQuery(id+"F4.opPattern","COPY",FACE,{"derivedFrom":makeQuery(id+"F1.opExtrude","SWEPT_FACE",FACE,{"disambiguationData":[OSD([sQuery(id+"F0.wireOp",EDGE,"E1")])]}),"instanceName":"1"});
            var sketch = newSketch(context, id + "F6", { "sketchPlane" : qUnion([Q0])});
            skLineSegment(sketch, "E516.bottom", {"start": v(-250.76, 37.5) * mm, "end": v(-315.76, 37.5) * mm});
            skLineSegment(sketch, "E516.top", {"start": v(-250.76, 152.5) * mm, "end": v(-315.76, 152.5) * mm});
            skLineSegment(sketch, "E516.left", {"start": v(-250.76, 37.5) * mm, "end": v(-250.76, 152.5) * mm});
            skLineSegment(sketch, "E516.right", {"start": v(-315.76, 37.5) * mm, "end": v(-315.76, 152.5) * mm});
            skLineSegment(sketch, "E517.bottom", {"start": v(123.24, 37.5) * mm, "end": v(17.94, 37.5) * mm});
            skLineSegment(sketch, "E517.top", {"start": v(123.24, 152.5) * mm, "end": v(17.94, 152.5) * mm});
            skLineSegment(sketch, "E517.left", {"start": v(123.24, 37.5) * mm, "end": v(123.24, 152.5) * mm});
            skLineSegment(sketch, "E517.right", {"start": v(17.94, 37.5) * mm, "end": v(17.94, 152.5) * mm});
            skLineSegment(sketch, "E518.0.0", {"start": v(-496.96, 0) * mm, "end": v(-206.96, 0) * mm, "construction": true});
            skLineSegment(sketch, "E518.0.1", {"start": v(-206.96, 0) * mm, "end": v(-206.96, 190) * mm, "construction": true});
            skLineSegment(sketch, "E518.0.2", {"start": v(-206.96, 190) * mm, "end": v(-496.96, 190) * mm, "construction": true});
            skLineSegment(sketch, "E518.0.3", {"start": v(-496.96, 190) * mm, "end": v(-496.96, 0) * mm, "construction": true});
            skLineSegment(sketch, "E519.0.0", {"start": v(-122.96, 0) * mm, "end": v(167.04, 0) * mm, "construction": true});
            skLineSegment(sketch, "E519.0.1", {"start": v(167.04, 0) * mm, "end": v(167.04, 190) * mm, "construction": true});
            skLineSegment(sketch, "E519.0.2", {"start": v(167.04, 190) * mm, "end": v(-122.96, 190) * mm, "construction": true});
            skLineSegment(sketch, "E519.0.3", {"start": v(-122.96, 190) * mm, "end": v(-122.96, 0) * mm, "construction": true});
            skSolve(sketch);
        }
        {
            var Q0;
            Q0 = qSketchRegion(id + "F6", true);
            extrude(context, id + "F7", {"entities" : qUnion([Q0]), "operationType" : NewBodyOperationType.REMOVE, "oppositeDirection" : true, "depth" : 87 * mm});
        }
        {
            var Q0;
            Q0=qCreatedBy(makeId("Front.planeOp"),FACE);
            var sketch = newSketch(context, id + "F8", { "sketchPlane" : qUnion([Q0])});
            skLineSegment(sketch, "E520", {"start": v(344.3, 189.48) * mm, "end": v(344.3, -0.52) * mm});
            skLineSegment(sketch, "E521", {"start": v(344.3, -0.52) * mm, "end": v(534.3, -0.52) * mm});
            skLineSegment(sketch, "E522", {"start": v(534.3, -0.52) * mm, "end": v(534.3, 189.48) * mm});
            skLineSegment(sketch, "E523", {"start": v(534.3, 189.48) * mm, "end": v(344.3, 189.48) * mm});
            skLineSegment(sketch, "E524", {"start": v(379.3, 154.48) * mm, "end": v(379.3, 98.48) * mm});
            skLineSegment(sketch, "E525", {"start": v(379.3, 98.48) * mm, "end": v(435.3, 98.48) * mm});
            skLineSegment(sketch, "E526", {"start": v(435.3, 98.48) * mm, "end": v(435.3, 154.48) * mm});
            skLineSegment(sketch, "E527", {"start": v(435.3, 154.48) * mm, "end": v(379.3, 154.48) * mm});
            skLineSegment(sketch, "E528", {"start": v(443.3, 154.48) * mm, "end": v(443.3, 98.48) * mm});
            skLineSegment(sketch, "E529", {"start": v(443.3, 98.48) * mm, "end": v(499.3, 98.48) * mm});
            skLineSegment(sketch, "E530", {"start": v(499.3, 98.48) * mm, "end": v(499.3, 154.48) * mm});
            skLineSegment(sketch, "E531", {"start": v(499.3, 154.48) * mm, "end": v(443.3, 154.48) * mm});
            skLineSegment(sketch, "E532", {"start": v(379.3, 90.48) * mm, "end": v(379.3, 34.48) * mm});
            skLineSegment(sketch, "E533", {"start": v(379.3, 34.48) * mm, "end": v(435.3, 34.48) * mm});
            skLineSegment(sketch, "E534", {"start": v(435.3, 34.48) * mm, "end": v(435.3, 90.48) * mm});
            skLineSegment(sketch, "E535", {"start": v(435.3, 90.48) * mm, "end": v(379.3, 90.48) * mm});
            skLineSegment(sketch, "E536", {"start": v(443.3, 90.48) * mm, "end": v(443.3, 34.48) * mm});
            skLineSegment(sketch, "E537", {"start": v(443.3, 34.48) * mm, "end": v(499.3, 34.48) * mm});
            skLineSegment(sketch, "E538", {"start": v(499.3, 34.48) * mm, "end": v(499.3, 90.48) * mm});
            skLineSegment(sketch, "E539", {"start": v(499.3, 90.48) * mm, "end": v(443.3, 90.48) * mm});
            skLineSegment(sketch, "E540", {"start": v(379.3, 180.48) * mm, "end": v(379.3, 162.48) * mm});
            skLineSegment(sketch, "E541", {"start": v(379.3, 162.48) * mm, "end": v(413.97, 162.48) * mm});
            skLineSegment(sketch, "E542", {"start": v(413.97, 162.48) * mm, "end": v(413.97, 180.48) * mm});
            skLineSegment(sketch, "E543", {"start": v(413.97, 180.48) * mm, "end": v(379.3, 180.48) * mm});
            skLineSegment(sketch, "E544", {"start": v(421.97, 180.48) * mm, "end": v(421.97, 162.48) * mm});
            skLineSegment(sketch, "E545", {"start": v(421.97, 162.48) * mm, "end": v(456.63, 162.48) * mm});
            skLineSegment(sketch, "E546", {"start": v(456.63, 162.48) * mm, "end": v(456.63, 180.48) * mm});
            skLineSegment(sketch, "E547", {"start": v(456.63, 180.48) * mm, "end": v(421.97, 180.48) * mm});
            skLineSegment(sketch, "E548", {"start": v(464.63, 180.48) * mm, "end": v(464.63, 162.48) * mm});
            skLineSegment(sketch, "E549", {"start": v(464.63, 162.48) * mm, "end": v(499.3, 162.48) * mm});
            skLineSegment(sketch, "E550", {"start": v(499.3, 162.48) * mm, "end": v(499.3, 180.48) * mm});
            skLineSegment(sketch, "E551", {"start": v(499.3, 180.48) * mm, "end": v(464.63, 180.48) * mm});
            skLineSegment(sketch, "E552", {"start": v(353.3, 154.48) * mm, "end": v(353.3, 119.81) * mm});
            skLineSegment(sketch, "E553", {"start": v(353.3, 119.81) * mm, "end": v(371.3, 119.81) * mm});
            skLineSegment(sketch, "E554", {"start": v(371.3, 119.81) * mm, "end": v(371.3, 154.48) * mm});
            skLineSegment(sketch, "E555", {"start": v(371.3, 154.48) * mm, "end": v(353.3, 154.48) * mm});
            skLineSegment(sketch, "E556", {"start": v(353.3, 111.81) * mm, "end": v(353.3, 77.15) * mm});
            skLineSegment(sketch, "E557", {"start": v(353.3, 77.15) * mm, "end": v(371.3, 77.15) * mm});
            skLineSegment(sketch, "E558", {"start": v(371.3, 77.15) * mm, "end": v(371.3, 111.81) * mm});
            skLineSegment(sketch, "E559", {"start": v(371.3, 111.81) * mm, "end": v(353.3, 111.81) * mm});
            skLineSegment(sketch, "E560", {"start": v(353.3, 69.15) * mm, "end": v(353.3, 34.48) * mm});
            skLineSegment(sketch, "E561", {"start": v(353.3, 34.48) * mm, "end": v(371.3, 34.48) * mm});
            skLineSegment(sketch, "E562", {"start": v(371.3, 34.48) * mm, "end": v(371.3, 69.15) * mm});
            skLineSegment(sketch, "E563", {"start": v(371.3, 69.15) * mm, "end": v(353.3, 69.15) * mm});
            skLineSegment(sketch, "E564", {"start": v(379.3, 26.48) * mm, "end": v(379.3, 8.48) * mm});
            skLineSegment(sketch, "E565", {"start": v(379.3, 8.48) * mm, "end": v(413.97, 8.48) * mm});
            skLineSegment(sketch, "E566", {"start": v(413.97, 8.48) * mm, "end": v(413.97, 26.48) * mm});
            skLineSegment(sketch, "E567", {"start": v(413.97, 26.48) * mm, "end": v(379.3, 26.48) * mm});
            skLineSegment(sketch, "E568", {"start": v(421.97, 26.48) * mm, "end": v(421.97, 8.48) * mm});
            skLineSegment(sketch, "E569", {"start": v(421.97, 8.48) * mm, "end": v(456.63, 8.48) * mm});
            skLineSegment(sketch, "E570", {"start": v(456.63, 8.48) * mm, "end": v(456.63, 26.48) * mm});
            skLineSegment(sketch, "E571", {"start": v(456.63, 26.48) * mm, "end": v(421.97, 26.48) * mm});
            skLineSegment(sketch, "E572", {"start": v(464.63, 26.48) * mm, "end": v(464.63, 8.48) * mm});
            skLineSegment(sketch, "E573", {"start": v(464.63, 8.48) * mm, "end": v(499.3, 8.48) * mm});
            skLineSegment(sketch, "E574", {"start": v(499.3, 8.48) * mm, "end": v(499.3, 26.48) * mm});
            skLineSegment(sketch, "E575", {"start": v(499.3, 26.48) * mm, "end": v(464.63, 26.48) * mm});
            skLineSegment(sketch, "E576", {"start": v(507.3, 154.48) * mm, "end": v(507.3, 119.81) * mm});
            skLineSegment(sketch, "E577", {"start": v(507.3, 119.81) * mm, "end": v(525.3, 119.81) * mm});
            skLineSegment(sketch, "E578", {"start": v(525.3, 119.81) * mm, "end": v(525.3, 154.48) * mm});
            skLineSegment(sketch, "E579", {"start": v(525.3, 154.48) * mm, "end": v(507.3, 154.48) * mm});
            skLineSegment(sketch, "E580", {"start": v(507.3, 111.81) * mm, "end": v(507.3, 77.15) * mm});
            skLineSegment(sketch, "E581", {"start": v(507.3, 77.15) * mm, "end": v(525.3, 77.15) * mm});
            skLineSegment(sketch, "E582", {"start": v(525.3, 77.15) * mm, "end": v(525.3, 111.81) * mm});
            skLineSegment(sketch, "E583", {"start": v(525.3, 111.81) * mm, "end": v(507.3, 111.81) * mm});
            skLineSegment(sketch, "E584", {"start": v(507.3, 69.15) * mm, "end": v(507.3, 34.48) * mm});
            skLineSegment(sketch, "E585", {"start": v(507.3, 34.48) * mm, "end": v(525.3, 34.48) * mm});
            skLineSegment(sketch, "E586", {"start": v(525.3, 34.48) * mm, "end": v(525.3, 69.15) * mm});
            skLineSegment(sketch, "E587", {"start": v(525.3, 69.15) * mm, "end": v(507.3, 69.15) * mm});
            skLineSegment(sketch, "E588", {"start": v(696.67, 100.73) * mm, "end": v(718.26, 100.73) * mm});
            skLineSegment(sketch, "E589", {"start": v(718.26, 100.73) * mm, "end": v(721.67, 25.73) * mm});
            skLineSegment(sketch, "E590", {"start": v(721.67, 25.73) * mm, "end": v(861.67, 25.73) * mm});
            skLineSegment(sketch, "E591", {"start": v(861.67, 25.73) * mm, "end": v(865.08, 100.73) * mm});
            skLineSegment(sketch, "E592", {"start": v(865.08, 100.73) * mm, "end": v(886.67, 100.73) * mm});
            skLineSegment(sketch, "E593", {"start": v(886.67, 100.73) * mm, "end": v(886.67, 0.73) * mm});
            skLineSegment(sketch, "E594", {"start": v(886.67, 0.73) * mm, "end": v(696.67, 0.73) * mm});
            skLineSegment(sketch, "E595", {"start": v(696.67, 0.73) * mm, "end": v(696.67, 100.73) * mm});
            skLineSegment(sketch, "E596", {"start": v(1096.67, 101.7) * mm, "end": v(1118.26, 101.7) * mm});
            skLineSegment(sketch, "E597", {"start": v(1118.26, 101.7) * mm, "end": v(1121.67, 26.7) * mm});
            skLineSegment(sketch, "E598", {"start": v(1121.67, 26.7) * mm, "end": v(1261.67, 26.7) * mm});
            skLineSegment(sketch, "E599", {"start": v(1261.67, 26.7) * mm, "end": v(1269.17, 191.7) * mm});
            skLineSegment(sketch, "E600", {"start": v(1269.17, 191.7) * mm, "end": v(1286.67, 191.7) * mm});
            skLineSegment(sketch, "E601", {"start": v(1286.67, 191.7) * mm, "end": v(1286.67, 1.7) * mm});
            skLineSegment(sketch, "E602", {"start": v(1286.67, 1.7) * mm, "end": v(1096.67, 1.7) * mm});
            skLineSegment(sketch, "E603", {"start": v(1096.67, 1.7) * mm, "end": v(1096.67, 101.7) * mm});
            skLineSegment(sketch, "E604", {"start": v(1444.84, 189.72) * mm, "end": v(1462.34, 189.72) * mm});
            skLineSegment(sketch, "E605", {"start": v(1462.34, 189.72) * mm, "end": v(1469.84, 24.72) * mm});
            skLineSegment(sketch, "E606", {"start": v(1469.84, 24.72) * mm, "end": v(1609.84, 24.72) * mm});
            skLineSegment(sketch, "E607", {"start": v(1609.84, 24.72) * mm, "end": v(1617.34, 189.72) * mm});
            skLineSegment(sketch, "E608", {"start": v(1617.34, 189.72) * mm, "end": v(1634.84, 189.72) * mm});
            skLineSegment(sketch, "E609", {"start": v(1634.84, 189.72) * mm, "end": v(1634.84, -0.28) * mm});
            skLineSegment(sketch, "E610", {"start": v(1634.84, -0.28) * mm, "end": v(1444.84, -0.28) * mm});
            skLineSegment(sketch, "E611", {"start": v(1444.84, -0.28) * mm, "end": v(1444.84, 189.72) * mm});
            skArc(sketch, "E612.cCircle", {"start": v(371.3, 171.48) * mm, "mid": v(355.94, 177.84) * mm, "end": v(362.3, 162.48) * mm});
            skPoint(sketch, "E612.cCircle.centerSnap0", {"position": v(362.3, 154.48) * mm});
            skPoint(sketch, "E612.cCircle.centerSnap1", {"position": v(379.3, 171.48) * mm});
            skLineSegment(sketch, "E612.0", {"start": v(371.3, 162.48) * mm, "end": v(362.3, 162.48) * mm});
            skLineSegment(sketch, "E612.3", {"start": v(371.3, 171.48) * mm, "end": v(371.3, 162.48) * mm});
            skPoint(sketch, "E612.0.midPoint", {"position": v(362.3, 162.48) * mm});
            skPoint(sketch, "E613.orphan", {"position": v(353.3, 180.48) * mm});
            skPoint(sketch, "E614.orphan", {"position": v(371.3, 180.48) * mm});
            skPoint(sketch, "E612.1.start.orphan", {"position": v(353.3, 162.48) * mm});
            skArc(sketch, "E615.cCircle", {"start": v(362.3, 26.48) * mm, "mid": v(355.94, 11.12) * mm, "end": v(371.3, 17.48) * mm});
            skPoint(sketch, "E615.cCircle.centerSnap0", {"position": v(362.3, 34.48) * mm});
            skPoint(sketch, "E615.cCircle.centerSnap1", {"position": v(379.3, 17.48) * mm});
            skLineSegment(sketch, "E615.0", {"start": v(362.3, 26.48) * mm, "end": v(371.3, 26.48) * mm});
            skLineSegment(sketch, "E615.1", {"start": v(371.3, 26.48) * mm, "end": v(371.3, 17.48) * mm});
            skPoint(sketch, "E615.0.midPoint", {"position": v(362.3, 26.48) * mm});
            skPoint(sketch, "E616.orphan", {"position": v(353.3, 8.48) * mm});
            skPoint(sketch, "E617.orphan", {"position": v(353.3, 26.48) * mm});
            skArc(sketch, "E618.cCircle", {"start": v(507.3, 17.48) * mm, "mid": v(522.66, 11.12) * mm, "end": v(516.3, 26.48) * mm});
            skPoint(sketch, "E618.cCircle.centerSnap0", {"position": v(516.3, 34.48) * mm});
            skPoint(sketch, "E618.cCircle.centerSnap1", {"position": v(499.3, 17.48) * mm});
            skLineSegment(sketch, "E618.0", {"start": v(507.3, 26.48) * mm, "end": v(516.3, 26.48) * mm});
            skLineSegment(sketch, "E618.3", {"start": v(507.3, 17.48) * mm, "end": v(507.3, 26.48) * mm});
            skPoint(sketch, "E618.0.midPoint", {"position": v(516.3, 26.48) * mm});
            skPoint(sketch, "E619.orphan", {"position": v(507.3, 8.48) * mm});
            skPoint(sketch, "E620.orphan", {"position": v(525.3, 26.48) * mm});
            skArc(sketch, "E621.cCircle", {"start": v(516.3, 162.48) * mm, "mid": v(522.66, 177.84) * mm, "end": v(507.3, 171.48) * mm});
            skPoint(sketch, "E621.cCircle.centerSnap0", {"position": v(516.3, 154.48) * mm});
            skPoint(sketch, "E621.cCircle.centerSnap1", {"position": v(499.3, 171.48) * mm});
            skLineSegment(sketch, "E621.0", {"start": v(516.3, 162.48) * mm, "end": v(507.3, 162.48) * mm});
            skLineSegment(sketch, "E621.1", {"start": v(507.3, 162.48) * mm, "end": v(507.3, 171.48) * mm});
            skPoint(sketch, "E621.0.midPoint", {"position": v(516.3, 162.48) * mm});
            skPoint(sketch, "E622.orphan", {"position": v(525.3, 180.48) * mm});
            skPoint(sketch, "E623.orphan", {"position": v(525.3, 162.48) * mm});
            skSolve(sketch);
        }
        {
            var Q0;
            Q0 = qSketchRegion(id + "F8", true);
            extrude(context, id + "F9", {"entities" : qUnion([Q0]), "depth" : 290 * mm});
        }
        {
            var Q0;
            Q0=makeQuery(id+"F9.opExtrude","SWEPT_BODY",BODY,{"disambiguationData":[OSD([sQuery(id+"F8.wireOp",EDGE,"E520"),sQuery(id+"F8.wireOp",EDGE,"E521"),sQuery(id+"F8.wireOp",EDGE,"E522"),sQuery(id+"F8.wireOp",EDGE,"E523"),sQuery(id+"F8.wireOp",EDGE,"E524"),sQuery(id+"F8.wireOp",EDGE,"E525"),sQuery(id+"F8.wireOp",EDGE,"E526"),sQuery(id+"F8.wireOp",EDGE,"E527"),sQuery(id+"F8.wireOp",EDGE,"E528"),sQuery(id+"F8.wireOp",EDGE,"E529"),sQuery(id+"F8.wireOp",EDGE,"E530"),sQuery(id+"F8.wireOp",EDGE,"E531"),sQuery(id+"F8.wireOp",EDGE,"E532"),sQuery(id+"F8.wireOp",EDGE,"E533"),sQuery(id+"F8.wireOp",EDGE,"E534"),sQuery(id+"F8.wireOp",EDGE,"E535"),sQuery(id+"F8.wireOp",EDGE,"E536"),sQuery(id+"F8.wireOp",EDGE,"E537"),sQuery(id+"F8.wireOp",EDGE,"E538"),sQuery(id+"F8.wireOp",EDGE,"E539"),sQuery(id+"F8.wireOp",EDGE,"E540"),sQuery(id+"F8.wireOp",EDGE,"E541"),sQuery(id+"F8.wireOp",EDGE,"E542"),sQuery(id+"F8.wireOp",EDGE,"E543"),sQuery(id+"F8.wireOp",EDGE,"E544"),sQuery(id+"F8.wireOp",EDGE,"E545"),sQuery(id+"F8.wireOp",EDGE,"E546"),sQuery(id+"F8.wireOp",EDGE,"E547"),sQuery(id+"F8.wireOp",EDGE,"E548"),sQuery(id+"F8.wireOp",EDGE,"E549"),sQuery(id+"F8.wireOp",EDGE,"E550"),sQuery(id+"F8.wireOp",EDGE,"E551"),sQuery(id+"F8.wireOp",EDGE,"E552"),sQuery(id+"F8.wireOp",EDGE,"E553"),sQuery(id+"F8.wireOp",EDGE,"E554"),sQuery(id+"F8.wireOp",EDGE,"E555"),sQuery(id+"F8.wireOp",EDGE,"E556"),sQuery(id+"F8.wireOp",EDGE,"E557"),sQuery(id+"F8.wireOp",EDGE,"E558"),sQuery(id+"F8.wireOp",EDGE,"E559"),sQuery(id+"F8.wireOp",EDGE,"E560"),sQuery(id+"F8.wireOp",EDGE,"E561"),sQuery(id+"F8.wireOp",EDGE,"E562"),sQuery(id+"F8.wireOp",EDGE,"E563"),sQuery(id+"F8.wireOp",EDGE,"E564"),sQuery(id+"F8.wireOp",EDGE,"E565"),sQuery(id+"F8.wireOp",EDGE,"E566"),sQuery(id+"F8.wireOp",EDGE,"E567"),sQuery(id+"F8.wireOp",EDGE,"E568"),sQuery(id+"F8.wireOp",EDGE,"E569"),sQuery(id+"F8.wireOp",EDGE,"E570"),sQuery(id+"F8.wireOp",EDGE,"E571"),sQuery(id+"F8.wireOp",EDGE,"E572"),sQuery(id+"F8.wireOp",EDGE,"E573"),sQuery(id+"F8.wireOp",EDGE,"E574"),sQuery(id+"F8.wireOp",EDGE,"E575"),sQuery(id+"F8.wireOp",EDGE,"E576"),sQuery(id+"F8.wireOp",EDGE,"E577"),sQuery(id+"F8.wireOp",EDGE,"E578"),sQuery(id+"F8.wireOp",EDGE,"E579"),sQuery(id+"F8.wireOp",EDGE,"E580"),sQuery(id+"F8.wireOp",EDGE,"E581"),sQuery(id+"F8.wireOp",EDGE,"E582"),sQuery(id+"F8.wireOp",EDGE,"E583"),sQuery(id+"F8.wireOp",EDGE,"E584"),sQuery(id+"F8.wireOp",EDGE,"E585"),sQuery(id+"F8.wireOp",EDGE,"E586"),sQuery(id+"F8.wireOp",EDGE,"E587")])]});
            var Q1;
            Q1=makeQuery(id+"F9.opExtrude","SWEPT_BODY",BODY,{"disambiguationData":[OSD([sQuery(id+"F8.wireOp",EDGE,"E588"),sQuery(id+"F8.wireOp",EDGE,"E589"),sQuery(id+"F8.wireOp",EDGE,"E590"),sQuery(id+"F8.wireOp",EDGE,"E591"),sQuery(id+"F8.wireOp",EDGE,"E592"),sQuery(id+"F8.wireOp",EDGE,"E593"),sQuery(id+"F8.wireOp",EDGE,"E594"),sQuery(id+"F8.wireOp",EDGE,"E595")])]});
            var Q2;
            Q2=makeQuery(id+"F9.opExtrude","SWEPT_BODY",BODY,{"disambiguationData":[OSD([sQuery(id+"F8.wireOp",EDGE,"E596"),sQuery(id+"F8.wireOp",EDGE,"E597"),sQuery(id+"F8.wireOp",EDGE,"E598"),sQuery(id+"F8.wireOp",EDGE,"E599"),sQuery(id+"F8.wireOp",EDGE,"E600"),sQuery(id+"F8.wireOp",EDGE,"E601"),sQuery(id+"F8.wireOp",EDGE,"E602"),sQuery(id+"F8.wireOp",EDGE,"E603")])]});
            var Q3;
            Q3=makeQuery(id+"F9.opExtrude","SWEPT_BODY",BODY,{"disambiguationData":[OSD([sQuery(id+"F8.wireOp",EDGE,"E604"),sQuery(id+"F8.wireOp",EDGE,"E605"),sQuery(id+"F8.wireOp",EDGE,"E606"),sQuery(id+"F8.wireOp",EDGE,"E607"),sQuery(id+"F8.wireOp",EDGE,"E608"),sQuery(id+"F8.wireOp",EDGE,"E609"),sQuery(id+"F8.wireOp",EDGE,"E610"),sQuery(id+"F8.wireOp",EDGE,"E611")])]});
            transform(context, id + "F10", {"entities" : qUnion([Q0, Q1, Q2, Q3]), "transformType" : TransformType.TRANSLATION_3D, "dx" : 0 * mm, "dy" : -198 * mm, "dz" : 0 * mm, "makeCopy" : false});
        }
    });
